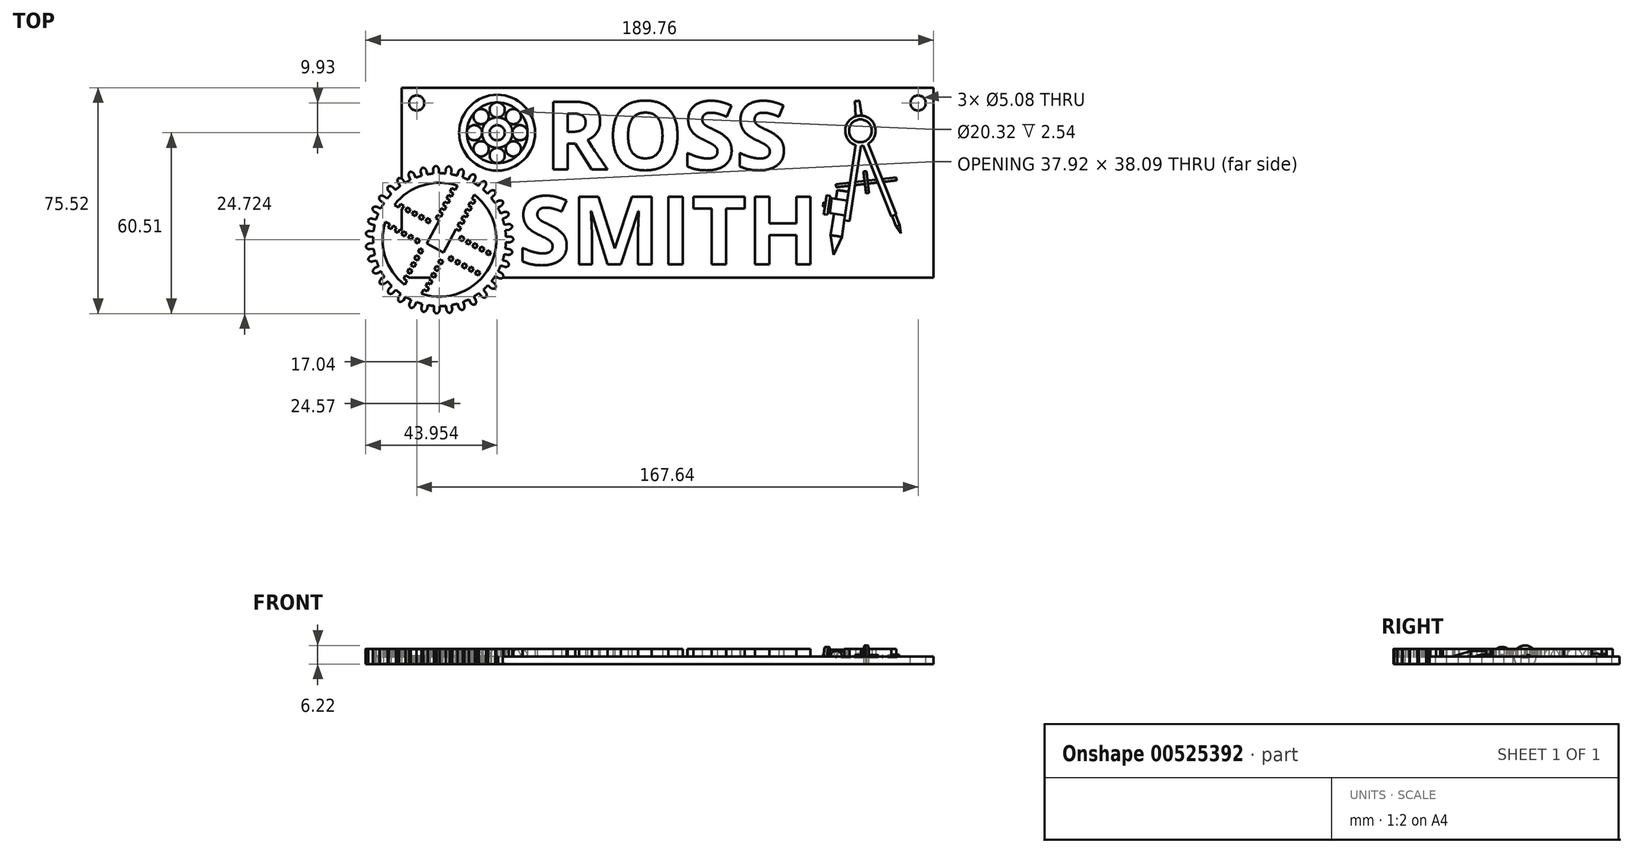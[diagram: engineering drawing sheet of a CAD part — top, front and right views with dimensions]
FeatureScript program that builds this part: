
annotation { "Feature Type Name" : "Feature", "Feature Type Description" : "" }
export const myFeature = defineFeature(function(context is Context, id is Id, definition is map)
    precondition{}
    {
        {
            var Q0;
            Q0=qCreatedBy(makeId("Top.planeOp"),FACE);
            var sketch = newSketch(context, id + "F0", { "sketchPlane" : qUnion([Q0])});
            skLineSegment(sketch, "E0.bottom", {"start": v(88.9, 31.75) * mm, "end": v(-88.9, 31.75) * mm});
            skLineSegment(sketch, "E0.top", {"start": v(88.9, -31.75) * mm, "end": v(-88.9, -31.75) * mm});
            skLineSegment(sketch, "E0.left", {"start": v(88.9, 31.75) * mm, "end": v(88.9, -31.75) * mm});
            skLineSegment(sketch, "E0.right", {"start": v(-88.9, 31.75) * mm, "end": v(-88.9, -31.75) * mm});
            skPoint(sketch, "E0.middle", {"position": v(0, 0) * mm});
            skSolve(sketch);
        }
        {
            var Q0;
            Q0=makeQuery(id+"F0.imprint","IMPRINT",FACE,{"disambiguationData":[TD([[makeQuery(id+"F0.imprint","IMPRINT",EDGE,{"derivedFrom":sQuery(id+"F0.wireOp",EDGE,"E0.bottom")}),1.0]])]});
            extrude(context, id + "F1", {"entities" : qUnion([Q0]), "depth" : 2.54 * mm, "offsetDistance" : 25.4 * mm});
        }
        {
            var Q0;
            Q0=makeQuery(id+"F1.opExtrude","CAP_FACE",FACE,{"disambiguationData":[OSD([sQuery(id+"F0.wireOp",EDGE,"E0.bottom"),sQuery(id+"F0.wireOp",EDGE,"E0.top"),sQuery(id+"F0.wireOp",EDGE,"E0.left"),sQuery(id+"F0.wireOp",EDGE,"E0.right")])],"isStart":false});
            var sketch = newSketch(context, id + "F2", { "sketchPlane" : qUnion([Q0])});
            skLineSegment(sketch, "E1.left", {"start": v(-49.9, -4.45) * mm, "end": v(-49.9, -27.3) * mm});
            skText(sketch, "E2", { "text": "ROSS", "fontName": "OpenSans-Bold.ttf"});
            skText(sketch, "E3", { "text": "SMITH", "fontName": "OpenSans-Bold.ttf"});
            const initialGuessF2  = {"E2": [-0.041, 0.00445, 1, 0, 0.02286], "E3": [-0.0499, -0.0273, 1, 0, 0.02286]};
            skSetInitialGuess(sketch, initialGuessF2);
            skSolve(sketch);
        }
        {
            var Q0;
            Q0 = qSketchRegion(id + "F2", true);
            extrude(context, id + "F3", {"entities" : qUnion([Q0]), "operationType" : NewBodyOperationType.ADD, "depth" : 2.54 * mm, "offsetDistance" : 25.4 * mm});
        }
        {
            var Q0;
            {var subQ0=sQuery(id+"F0.wireOp",EDGE,"E0.left");var subQ1=sQuery(id+"F0.wireOp",EDGE,"E0.top");var subQ2=sQuery(id+"F0.wireOp",EDGE,"E0.right");var subQ3=sQuery(id+"F0.wireOp",EDGE,"E0.bottom");Q0=makeQuery(id+"F3.boolean.opBoolean","SPLIT",FACE,{"disambiguationData":[TD([makeQuery(id+"F1.opExtrude","SWEPT_FACE",FACE,{"disambiguationData":[OSD([subQ3])]})])],"derivedFrom":makeQuery(id+"F1.opExtrude","CAP_FACE",FACE,{"disambiguationData":[OSD([subQ3,subQ1,subQ0,subQ2])],"isStart":false})});}
            var sketch = newSketch(context, id + "F4", { "sketchPlane" : qUnion([Q0])});
            skCircle(sketch, "E4", {"center": v(-76.2, -19.05) * mm, "radius": 22.23 * mm});
            skLineSegment(sketch, "E5.bottom", {"start": v(-71.9, -17.74) * mm, "end": v(-77.51, -14.76) * mm});
            skLineSegment(sketch, "E5.top", {"start": v(-74.89, -23.34) * mm, "end": v(-80.5, -20.36) * mm});
            skLineSegment(sketch, "E5.left", {"start": v(-71.9, -17.74) * mm, "end": v(-74.89, -23.34) * mm});
            skLineSegment(sketch, "E5.right", {"start": v(-77.51, -14.76) * mm, "end": v(-80.5, -20.36) * mm});
            skCircle(sketch, "E6", {"center": v(-76.2, -19.05) * mm, "radius": 19.05 * mm});
            skLineSegment(sketch, "E7", {"start": v(-77.51, -14.76) * mm, "end": v(-70.19, -0.97) * mm});
            skLineSegment(sketch, "E8", {"start": v(-71.9, -17.74) * mm, "end": v(-64.58, -3.96) * mm});
            skLineSegment(sketch, "E9.bottom", {"start": v(-71.9, -17.74) * mm, "end": v(-70.78, -18.33) * mm});
            skLineSegment(sketch, "E9.top", {"start": v(-71.3, -16.62) * mm, "end": v(-70.19, -17.21) * mm});
            skLineSegment(sketch, "E9.left", {"start": v(-71.9, -17.74) * mm, "end": v(-71.3, -16.62) * mm});
            skLineSegment(sketch, "E9.right", {"start": v(-70.78, -18.33) * mm, "end": v(-70.19, -17.21) * mm});
            skLineSegment(sketch, "E10.bottom", {"start": v(-77.51, -14.76) * mm, "end": v(-78.63, -14.16) * mm});
            skLineSegment(sketch, "E10.top", {"start": v(-76.92, -13.63) * mm, "end": v(-78.04, -13.04) * mm});
            skLineSegment(sketch, "E10.left", {"start": v(-77.51, -14.76) * mm, "end": v(-76.92, -13.63) * mm});
            skLineSegment(sketch, "E10.right", {"start": v(-78.63, -14.16) * mm, "end": v(-78.04, -13.04) * mm});
            skLineSegment(sketch, "E11.0.1.0", {"start": v(-70.71, -15.5) * mm, "end": v(-69.6, -16.1) * mm});
            skLineSegment(sketch, "E11.0.1.1", {"start": v(-70.12, -14.37) * mm, "end": v(-69, -14.97) * mm});
            skLineSegment(sketch, "E11.0.1.2", {"start": v(-69.6, -16.1) * mm, "end": v(-69, -14.97) * mm});
            skLineSegment(sketch, "E11.0.1.3", {"start": v(-75.72, -11.4) * mm, "end": v(-76.85, -10.8) * mm});
            skLineSegment(sketch, "E11.0.1.4", {"start": v(-77.44, -11.92) * mm, "end": v(-76.85, -10.8) * mm});
            skLineSegment(sketch, "E11.0.1.5", {"start": v(-76.32, -12.51) * mm, "end": v(-77.44, -11.92) * mm});
            skLineSegment(sketch, "E11.0.2.0", {"start": v(-69.52, -13.25) * mm, "end": v(-68.4, -13.85) * mm});
            skLineSegment(sketch, "E11.0.2.1", {"start": v(-68.92, -12.13) * mm, "end": v(-67.8, -12.73) * mm});
            skLineSegment(sketch, "E11.0.2.2", {"start": v(-68.4, -13.85) * mm, "end": v(-67.8, -12.73) * mm});
            skLineSegment(sketch, "E11.0.2.3", {"start": v(-74.53, -9.15) * mm, "end": v(-75.65, -8.55) * mm});
            skLineSegment(sketch, "E11.0.2.4", {"start": v(-76.25, -9.67) * mm, "end": v(-75.65, -8.55) * mm});
            skLineSegment(sketch, "E11.0.2.5", {"start": v(-75.13, -10.27) * mm, "end": v(-76.25, -9.67) * mm});
            skLineSegment(sketch, "E11.0.3.0", {"start": v(-68.33, -11) * mm, "end": v(-67.2, -11.6) * mm});
            skLineSegment(sketch, "E11.0.3.1", {"start": v(-67.73, -9.89) * mm, "end": v(-66.61, -10.48) * mm});
            skLineSegment(sketch, "E11.0.3.2", {"start": v(-67.2, -11.6) * mm, "end": v(-66.61, -10.48) * mm});
            skLineSegment(sketch, "E11.0.3.3", {"start": v(-73.34, -6.9) * mm, "end": v(-74.46, -6.31) * mm});
            skLineSegment(sketch, "E11.0.3.4", {"start": v(-75.06, -7.43) * mm, "end": v(-74.46, -6.31) * mm});
            skLineSegment(sketch, "E11.0.3.5", {"start": v(-73.94, -8.03) * mm, "end": v(-75.06, -7.43) * mm});
            skLineSegment(sketch, "E11.0.4.0", {"start": v(-67.14, -8.77) * mm, "end": v(-66.01, -9.36) * mm});
            skLineSegment(sketch, "E11.0.4.1", {"start": v(-66.54, -7.65) * mm, "end": v(-65.42, -8.24) * mm});
            skLineSegment(sketch, "E11.0.4.2", {"start": v(-66.01, -9.36) * mm, "end": v(-65.42, -8.24) * mm});
            skLineSegment(sketch, "E11.0.4.3", {"start": v(-72.15, -4.66) * mm, "end": v(-73.27, -4.07) * mm});
            skLineSegment(sketch, "E11.0.4.4", {"start": v(-73.86, -5.19) * mm, "end": v(-73.27, -4.07) * mm});
            skLineSegment(sketch, "E11.0.4.5", {"start": v(-72.74, -5.79) * mm, "end": v(-73.86, -5.19) * mm});
            skLineSegment(sketch, "E11.0.5.0", {"start": v(-65.94, -6.52) * mm, "end": v(-64.82, -7.12) * mm});
            skLineSegment(sketch, "E11.0.5.1", {"start": v(-65.35, -5.4) * mm, "end": v(-64.23, -6) * mm});
            skLineSegment(sketch, "E11.0.5.2", {"start": v(-64.82, -7.12) * mm, "end": v(-64.23, -6) * mm});
            skLineSegment(sketch, "E11.0.5.3", {"start": v(-70.95, -2.42) * mm, "end": v(-72.08, -1.83) * mm});
            skLineSegment(sketch, "E11.0.5.4", {"start": v(-72.67, -2.95) * mm, "end": v(-72.08, -1.83) * mm});
            skLineSegment(sketch, "E11.0.5.5", {"start": v(-71.55, -3.54) * mm, "end": v(-72.67, -2.95) * mm});
            skLineSegment(sketch, "E11.direction1", {"start": v(-78.63, -14.16) * mm, "end": v(-56.2, -26.08) * mm, "construction": true});
            skLineSegment(sketch, "E11.direction2", {"start": v(-78.63, -14.16) * mm, "end": v(-77.44, -11.92) * mm, "construction": true});
            skLineSegment(sketch, "E12.1.0", {"start": v(-77.51, -14.76) * mm, "end": v(-91.3, -7.43) * mm});
            skLineSegment(sketch, "E12.1.1", {"start": v(-80.5, -20.36) * mm, "end": v(-94.28, -13.04) * mm});
            skLineSegment(sketch, "E12.1.2", {"start": v(-91.7, -14.4) * mm, "end": v(-92.3, -15.52) * mm});
            skLineSegment(sketch, "E12.1.3", {"start": v(-82.74, -19.17) * mm, "end": v(-83.33, -20.3) * mm});
            skLineSegment(sketch, "E12.1.4", {"start": v(-83.64, -10.06) * mm, "end": v(-84.77, -9.46) * mm});
            skLineSegment(sketch, "E12.1.5", {"start": v(-90.59, -15) * mm, "end": v(-91.18, -16.12) * mm});
            skLineSegment(sketch, "E12.1.6", {"start": v(-80.5, -20.36) * mm, "end": v(-81.1, -21.48) * mm});
            skLineSegment(sketch, "E12.1.8", {"start": v(-92.3, -15.52) * mm, "end": v(-93.42, -14.93) * mm});
            skLineSegment(sketch, "E12.1.11", {"start": v(-80.5, -20.36) * mm, "end": v(-81.62, -19.77) * mm});
            skLineSegment(sketch, "E12.1.12", {"start": v(-85.58, -19.1) * mm, "end": v(-86.7, -18.5) * mm});
            skLineSegment(sketch, "E12.1.13", {"start": v(-89.46, -15.6) * mm, "end": v(-90.06, -16.71) * mm});
            skLineSegment(sketch, "E12.1.14", {"start": v(-88.13, -7.67) * mm, "end": v(-89.25, -7.08) * mm});
            skLineSegment(sketch, "E12.1.15", {"start": v(-87.82, -17.9) * mm, "end": v(-88.94, -17.31) * mm});
            skLineSegment(sketch, "E12.1.16", {"start": v(-81.1, -21.48) * mm, "end": v(-83.33, -20.3) * mm, "construction": true});
            skLineSegment(sketch, "E12.1.17", {"start": v(-88.34, -16.19) * mm, "end": v(-88.94, -17.31) * mm});
            skLineSegment(sketch, "E12.1.18", {"start": v(-83.86, -18.57) * mm, "end": v(-84.45, -19.7) * mm});
            skLineSegment(sketch, "E12.1.19", {"start": v(-81.4, -11.25) * mm, "end": v(-82.52, -10.65) * mm});
            skLineSegment(sketch, "E12.1.20", {"start": v(-87.22, -16.79) * mm, "end": v(-87.82, -17.9) * mm});
            skLineSegment(sketch, "E12.1.21", {"start": v(-92.83, -13.8) * mm, "end": v(-93.42, -14.93) * mm});
            skLineSegment(sketch, "E12.1.22", {"start": v(-84.98, -17.98) * mm, "end": v(-85.58, -19.1) * mm});
            skLineSegment(sketch, "E12.1.23", {"start": v(-83.33, -20.3) * mm, "end": v(-84.45, -19.7) * mm});
            skLineSegment(sketch, "E12.1.24", {"start": v(-79.16, -12.44) * mm, "end": v(-80.28, -11.85) * mm});
            skLineSegment(sketch, "E12.1.25", {"start": v(-86.1, -17.38) * mm, "end": v(-86.7, -18.5) * mm});
            skLineSegment(sketch, "E12.1.26", {"start": v(-81.62, -19.77) * mm, "end": v(-82.21, -20.89) * mm});
            skLineSegment(sketch, "E12.1.27", {"start": v(-84.24, -11.18) * mm, "end": v(-83.64, -10.06) * mm});
            skLineSegment(sketch, "E12.1.28", {"start": v(-81.1, -21.48) * mm, "end": v(-82.21, -20.89) * mm});
            skLineSegment(sketch, "E12.1.29", {"start": v(-87.6, -9.4) * mm, "end": v(-87, -8.27) * mm});
            skLineSegment(sketch, "E12.1.30", {"start": v(-83.12, -11.77) * mm, "end": v(-82.52, -10.65) * mm});
            skLineSegment(sketch, "E12.1.31", {"start": v(-79.76, -13.56) * mm, "end": v(-79.16, -12.44) * mm});
            skLineSegment(sketch, "E12.1.32", {"start": v(-82, -12.37) * mm, "end": v(-81.4, -11.25) * mm});
            skLineSegment(sketch, "E12.1.33", {"start": v(-88.73, -8.8) * mm, "end": v(-88.13, -7.67) * mm});
            skLineSegment(sketch, "E12.1.34", {"start": v(-85.36, -10.58) * mm, "end": v(-84.77, -9.46) * mm});
            skLineSegment(sketch, "E12.1.35", {"start": v(-80.88, -12.97) * mm, "end": v(-80.28, -11.85) * mm});
            skLineSegment(sketch, "E12.1.36", {"start": v(-86.48, -9.99) * mm, "end": v(-85.89, -8.86) * mm});
            skLineSegment(sketch, "E12.1.37", {"start": v(-89.85, -8.2) * mm, "end": v(-89.25, -7.08) * mm});
            skLineSegment(sketch, "E12.1.40", {"start": v(-90.06, -16.71) * mm, "end": v(-91.18, -16.12) * mm});
            skLineSegment(sketch, "E12.1.41", {"start": v(-85.89, -8.86) * mm, "end": v(-87, -8.27) * mm});
            skLineSegment(sketch, "E12.2.0", {"start": v(-80.5, -20.36) * mm, "end": v(-87.82, -34.14) * mm});
            skLineSegment(sketch, "E12.2.1", {"start": v(-74.89, -23.34) * mm, "end": v(-82.21, -37.13) * mm});
            skLineSegment(sketch, "E12.2.2", {"start": v(-80.85, -34.56) * mm, "end": v(-79.73, -35.15) * mm});
            skLineSegment(sketch, "E12.2.3", {"start": v(-76.08, -25.59) * mm, "end": v(-74.96, -26.18) * mm});
            skLineSegment(sketch, "E12.2.4", {"start": v(-85.2, -26.5) * mm, "end": v(-85.79, -27.62) * mm});
            skLineSegment(sketch, "E12.2.5", {"start": v(-80.25, -33.44) * mm, "end": v(-79.13, -34.03) * mm});
            skLineSegment(sketch, "E12.2.6", {"start": v(-74.89, -23.34) * mm, "end": v(-73.77, -23.94) * mm});
            skLineSegment(sketch, "E12.2.7", {"start": v(-81.62, -19.77) * mm, "end": v(-82.21, -20.89) * mm});
            skLineSegment(sketch, "E12.2.8", {"start": v(-79.73, -35.15) * mm, "end": v(-80.32, -36.27) * mm});
            skLineSegment(sketch, "E12.2.9", {"start": v(-80.5, -20.36) * mm, "end": v(-81.1, -21.48) * mm});
            skLineSegment(sketch, "E12.2.10", {"start": v(-80.5, -20.36) * mm, "end": v(-74.89, -23.34) * mm});
            skLineSegment(sketch, "E12.2.11", {"start": v(-74.89, -23.34) * mm, "end": v(-75.48, -24.47) * mm});
            skLineSegment(sketch, "E12.2.12", {"start": v(-76.15, -28.43) * mm, "end": v(-76.75, -29.55) * mm});
            skLineSegment(sketch, "E12.2.13", {"start": v(-79.66, -32.31) * mm, "end": v(-78.54, -32.91) * mm});
            skLineSegment(sketch, "E12.2.14", {"start": v(-87.58, -30.98) * mm, "end": v(-88.17, -32.1) * mm});
            skLineSegment(sketch, "E12.2.15", {"start": v(-77.34, -30.67) * mm, "end": v(-77.94, -31.79) * mm});
            skLineSegment(sketch, "E12.2.16", {"start": v(-73.77, -23.94) * mm, "end": v(-74.96, -26.18) * mm, "construction": true});
            skLineSegment(sketch, "E12.2.17", {"start": v(-79.06, -31.2) * mm, "end": v(-77.94, -31.79) * mm});
            skLineSegment(sketch, "E12.2.18", {"start": v(-76.68, -26.7) * mm, "end": v(-75.55, -27.3) * mm});
            skLineSegment(sketch, "E12.2.19", {"start": v(-84, -24.25) * mm, "end": v(-84.6, -25.37) * mm});
            skLineSegment(sketch, "E12.2.20", {"start": v(-78.46, -30.07) * mm, "end": v(-77.34, -30.67) * mm});
            skLineSegment(sketch, "E12.2.21", {"start": v(-81.45, -35.68) * mm, "end": v(-80.32, -36.27) * mm});
            skLineSegment(sketch, "E12.2.22", {"start": v(-77.27, -27.83) * mm, "end": v(-76.15, -28.43) * mm});
            skLineSegment(sketch, "E12.2.23", {"start": v(-74.96, -26.18) * mm, "end": v(-75.55, -27.3) * mm});
            skLineSegment(sketch, "E12.2.24", {"start": v(-82.8, -22) * mm, "end": v(-83.4, -23.13) * mm});
            skLineSegment(sketch, "E12.2.25", {"start": v(-77.87, -28.95) * mm, "end": v(-76.75, -29.55) * mm});
            skLineSegment(sketch, "E12.2.26", {"start": v(-75.48, -24.47) * mm, "end": v(-74.36, -25.06) * mm});
            skLineSegment(sketch, "E12.2.27", {"start": v(-84.07, -27.1) * mm, "end": v(-85.2, -26.5) * mm});
            skLineSegment(sketch, "E12.2.28", {"start": v(-73.77, -23.94) * mm, "end": v(-74.36, -25.06) * mm});
            skLineSegment(sketch, "E12.2.29", {"start": v(-85.86, -30.45) * mm, "end": v(-86.98, -29.86) * mm});
            skLineSegment(sketch, "E12.2.30", {"start": v(-83.48, -25.97) * mm, "end": v(-84.6, -25.37) * mm});
            skLineSegment(sketch, "E12.2.31", {"start": v(-81.69, -22.6) * mm, "end": v(-82.8, -22) * mm});
            skLineSegment(sketch, "E12.2.32", {"start": v(-82.88, -24.85) * mm, "end": v(-84, -24.25) * mm});
            skLineSegment(sketch, "E12.2.33", {"start": v(-86.46, -31.58) * mm, "end": v(-87.58, -30.98) * mm});
            skLineSegment(sketch, "E12.2.34", {"start": v(-84.67, -28.21) * mm, "end": v(-85.79, -27.62) * mm});
            skLineSegment(sketch, "E12.2.35", {"start": v(-82.28, -23.73) * mm, "end": v(-83.4, -23.13) * mm});
            skLineSegment(sketch, "E12.2.36", {"start": v(-85.26, -29.33) * mm, "end": v(-86.39, -28.74) * mm});
            skLineSegment(sketch, "E12.2.37", {"start": v(-87.05, -32.7) * mm, "end": v(-88.17, -32.1) * mm});
            skLineSegment(sketch, "E12.2.38", {"start": v(-81.1, -21.48) * mm, "end": v(-82.21, -20.89) * mm});
            skLineSegment(sketch, "E12.2.39", {"start": v(-80.5, -20.36) * mm, "end": v(-81.62, -19.77) * mm});
            skLineSegment(sketch, "E12.2.40", {"start": v(-78.54, -32.91) * mm, "end": v(-79.13, -34.03) * mm});
            skLineSegment(sketch, "E12.2.41", {"start": v(-86.39, -28.74) * mm, "end": v(-86.98, -29.86) * mm});
            skLineSegment(sketch, "E12.3.0", {"start": v(-74.89, -23.34) * mm, "end": v(-61.1, -30.67) * mm});
            skLineSegment(sketch, "E12.3.1", {"start": v(-71.9, -17.74) * mm, "end": v(-58.12, -25.06) * mm});
            skLineSegment(sketch, "E12.3.2", {"start": v(-60.7, -23.7) * mm, "end": v(-60.1, -22.58) * mm});
            skLineSegment(sketch, "E12.3.3", {"start": v(-69.66, -18.93) * mm, "end": v(-69.07, -17.8) * mm});
            skLineSegment(sketch, "E12.3.4", {"start": v(-68.76, -28.04) * mm, "end": v(-67.63, -28.64) * mm});
            skLineSegment(sketch, "E12.3.5", {"start": v(-61.81, -23.1) * mm, "end": v(-61.22, -21.98) * mm});
            skLineSegment(sketch, "E12.3.7", {"start": v(-75.48, -24.47) * mm, "end": v(-74.36, -25.06) * mm});
            skLineSegment(sketch, "E12.3.8", {"start": v(-60.1, -22.58) * mm, "end": v(-58.98, -23.17) * mm});
            skLineSegment(sketch, "E12.3.9", {"start": v(-74.89, -23.34) * mm, "end": v(-73.77, -23.94) * mm});
            skLineSegment(sketch, "E12.3.10", {"start": v(-74.89, -23.34) * mm, "end": v(-71.9, -17.74) * mm});
            skLineSegment(sketch, "E12.3.12", {"start": v(-66.82, -19) * mm, "end": v(-65.7, -19.6) * mm});
            skLineSegment(sketch, "E12.3.13", {"start": v(-62.94, -22.5) * mm, "end": v(-62.34, -21.39) * mm});
            skLineSegment(sketch, "E12.3.14", {"start": v(-64.27, -30.43) * mm, "end": v(-63.15, -31.02) * mm});
            skLineSegment(sketch, "E12.3.15", {"start": v(-64.58, -20.2) * mm, "end": v(-63.46, -20.79) * mm});
            skLineSegment(sketch, "E12.3.16", {"start": v(-71.3, -16.62) * mm, "end": v(-69.07, -17.8) * mm, "construction": true});
            skLineSegment(sketch, "E12.3.17", {"start": v(-64.06, -21.91) * mm, "end": v(-63.46, -20.79) * mm});
            skLineSegment(sketch, "E12.3.18", {"start": v(-68.54, -19.53) * mm, "end": v(-67.95, -18.4) * mm});
            skLineSegment(sketch, "E12.3.19", {"start": v(-71, -26.85) * mm, "end": v(-69.88, -27.45) * mm});
            skLineSegment(sketch, "E12.3.20", {"start": v(-65.18, -21.31) * mm, "end": v(-64.58, -20.2) * mm});
            skLineSegment(sketch, "E12.3.21", {"start": v(-59.57, -24.3) * mm, "end": v(-58.98, -23.17) * mm});
            skLineSegment(sketch, "E12.3.22", {"start": v(-67.42, -20.12) * mm, "end": v(-66.82, -19) * mm});
            skLineSegment(sketch, "E12.3.23", {"start": v(-69.07, -17.8) * mm, "end": v(-67.95, -18.4) * mm});
            skLineSegment(sketch, "E12.3.24", {"start": v(-73.24, -25.66) * mm, "end": v(-72.12, -26.25) * mm});
            skLineSegment(sketch, "E12.3.25", {"start": v(-66.3, -20.72) * mm, "end": v(-65.7, -19.6) * mm});
            skLineSegment(sketch, "E12.3.27", {"start": v(-68.16, -26.92) * mm, "end": v(-68.76, -28.04) * mm});
            skLineSegment(sketch, "E12.3.29", {"start": v(-64.8, -28.7) * mm, "end": v(-65.4, -29.83) * mm});
            skLineSegment(sketch, "E12.3.30", {"start": v(-69.28, -26.33) * mm, "end": v(-69.88, -27.45) * mm});
            skLineSegment(sketch, "E12.3.31", {"start": v(-72.64, -24.54) * mm, "end": v(-73.24, -25.66) * mm});
            skLineSegment(sketch, "E12.3.32", {"start": v(-70.4, -25.73) * mm, "end": v(-71, -26.85) * mm});
            skLineSegment(sketch, "E12.3.33", {"start": v(-63.67, -29.3) * mm, "end": v(-64.27, -30.43) * mm});
            skLineSegment(sketch, "E12.3.34", {"start": v(-67.04, -27.52) * mm, "end": v(-67.63, -28.64) * mm});
            skLineSegment(sketch, "E12.3.35", {"start": v(-71.52, -25.13) * mm, "end": v(-72.12, -26.25) * mm});
            skLineSegment(sketch, "E12.3.36", {"start": v(-65.92, -28.11) * mm, "end": v(-66.51, -29.24) * mm});
            skLineSegment(sketch, "E12.3.37", {"start": v(-62.55, -29.9) * mm, "end": v(-63.15, -31.02) * mm});
            skLineSegment(sketch, "E12.3.38", {"start": v(-73.77, -23.94) * mm, "end": v(-74.36, -25.06) * mm});
            skLineSegment(sketch, "E12.3.39", {"start": v(-74.89, -23.34) * mm, "end": v(-75.48, -24.47) * mm});
            skLineSegment(sketch, "E12.3.40", {"start": v(-62.34, -21.39) * mm, "end": v(-61.22, -21.98) * mm});
            skLineSegment(sketch, "E12.3.41", {"start": v(-66.51, -29.24) * mm, "end": v(-65.4, -29.83) * mm});
            skLineSegment(sketch, "E13", {"start": v(-66.62, 1) * mm, "end": v(-64.93, 0.1) * mm});
            skPoint(sketch, "E14.positionSnap0", {"position": v(-74.7, -16.25) * mm});
            skPoint(sketch, "E15", {"position": v(-64.58, 2.8) * mm});
            skPoint(sketch, "E15.positionSnap0", {"position": v(-65.77, 0.55) * mm});
            skLineSegment(sketch, "E16", {"start": v(-66.62, 1) * mm, "end": v(-66.02, 2.12) * mm});
            skLineSegment(sketch, "E17", {"start": v(-64.93, 0.1) * mm, "end": v(-64.34, 1.23) * mm});
            skArc(sketch, "E18", {"start": v(-64.58, 2.8) * mm, "mid": v(-65.41, 2.7) * mm, "end": v(-66.02, 2.12) * mm});
            skArc(sketch, "E19", {"start": v(-64.34, 1.23) * mm, "mid": v(-64.2, 2.05) * mm, "end": v(-64.58, 2.8) * mm});
            skArc(sketch, "E20.1.0", {"start": v(-68.15, 3.02) * mm, "mid": v(-68.16, 3.86) * mm, "end": v(-68.67, 4.52) * mm});
            skArc(sketch, "E20.1.1", {"start": v(-68.67, 4.52) * mm, "mid": v(-69.47, 4.28) * mm, "end": v(-69.96, 3.6) * mm});
            skLineSegment(sketch, "E20.1.2", {"start": v(-70.35, 2.4) * mm, "end": v(-69.96, 3.6) * mm});
            skLineSegment(sketch, "E20.1.3", {"start": v(-68.54, 1.81) * mm, "end": v(-68.15, 3.02) * mm});
            skArc(sketch, "E20.2.0", {"start": v(-72.22, 4.1) * mm, "mid": v(-72.38, 4.93) * mm, "end": v(-73, 5.49) * mm});
            skArc(sketch, "E20.2.1", {"start": v(-73, 5.49) * mm, "mid": v(-73.74, 5.1) * mm, "end": v(-74.1, 4.35) * mm});
            skLineSegment(sketch, "E20.2.2", {"start": v(-74.27, 3.1) * mm, "end": v(-74.1, 4.35) * mm});
            skLineSegment(sketch, "E20.2.3", {"start": v(-72.38, 2.84) * mm, "end": v(-72.22, 4.1) * mm});
            skArc(sketch, "E20.3.0", {"start": v(-76.42, 4.44) * mm, "mid": v(-76.72, 5.22) * mm, "end": v(-77.43, 5.66) * mm});
            skArc(sketch, "E20.3.1", {"start": v(-77.43, 5.66) * mm, "mid": v(-78.1, 5.15) * mm, "end": v(-78.32, 4.35) * mm});
            skLineSegment(sketch, "E20.3.2", {"start": v(-78.26, 3.08) * mm, "end": v(-78.32, 4.35) * mm});
            skLineSegment(sketch, "E20.3.3", {"start": v(-76.35, 3.17) * mm, "end": v(-76.42, 4.44) * mm});
            skArc(sketch, "E20.4.0", {"start": v(-80.6, 4.03) * mm, "mid": v(-81.05, 4.74) * mm, "end": v(-81.82, 5.05) * mm});
            skArc(sketch, "E20.4.1", {"start": v(-81.82, 5.05) * mm, "mid": v(-82.39, 4.43) * mm, "end": v(-82.46, 3.6) * mm});
            skLineSegment(sketch, "E20.4.2", {"start": v(-82.17, 2.36) * mm, "end": v(-82.46, 3.6) * mm});
            skLineSegment(sketch, "E20.4.3", {"start": v(-80.32, 2.79) * mm, "end": v(-80.6, 4.03) * mm});
            skArc(sketch, "E20.5.0", {"start": v(-84.66, 2.87) * mm, "mid": v(-85.22, 3.5) * mm, "end": v(-86.04, 3.66) * mm});
            skArc(sketch, "E20.5.1", {"start": v(-86.04, 3.66) * mm, "mid": v(-86.48, 2.94) * mm, "end": v(-86.4, 2.11) * mm});
            skLineSegment(sketch, "E20.5.2", {"start": v(-85.9, 0.95) * mm, "end": v(-86.4, 2.11) * mm});
            skLineSegment(sketch, "E20.5.3", {"start": v(-84.15, 1.7) * mm, "end": v(-84.66, 2.87) * mm});
            skArc(sketch, "E20.6.0", {"start": v(-88.44, 1) * mm, "mid": v(-89.1, 1.52) * mm, "end": v(-89.93, 1.53) * mm});
            skArc(sketch, "E20.6.1", {"start": v(-89.93, 1.53) * mm, "mid": v(-90.24, 0.76) * mm, "end": v(-90.02, -0.05) * mm});
            skLineSegment(sketch, "E20.6.2", {"start": v(-89.32, -1.1) * mm, "end": v(-90.02, -0.05) * mm});
            skLineSegment(sketch, "E20.6.3", {"start": v(-87.73, -0.05) * mm, "end": v(-88.44, 1) * mm});
            skArc(sketch, "E20.7.0", {"start": v(-91.82, -1.5) * mm, "mid": v(-92.56, -1.11) * mm, "end": v(-93.39, -1.25) * mm});
            skArc(sketch, "E20.7.1", {"start": v(-93.39, -1.25) * mm, "mid": v(-93.55, -2.07) * mm, "end": v(-93.2, -2.82) * mm});
            skLineSegment(sketch, "E20.7.2", {"start": v(-92.3, -3.74) * mm, "end": v(-93.2, -2.82) * mm});
            skLineSegment(sketch, "E20.7.3", {"start": v(-90.94, -2.41) * mm, "end": v(-91.82, -1.5) * mm});
            skArc(sketch, "E20.8.0", {"start": v(-94.7, -4.57) * mm, "mid": v(-95.5, -4.32) * mm, "end": v(-96.3, -4.6) * mm});
            skArc(sketch, "E20.8.1", {"start": v(-96.3, -4.6) * mm, "mid": v(-96.3, -5.44) * mm, "end": v(-95.82, -6.12) * mm});
            skLineSegment(sketch, "E20.8.2", {"start": v(-94.78, -6.86) * mm, "end": v(-95.82, -6.12) * mm});
            skLineSegment(sketch, "E20.8.3", {"start": v(-93.67, -5.31) * mm, "end": v(-94.7, -4.57) * mm});
            skArc(sketch, "E20.9.0", {"start": v(-97, -8.1) * mm, "mid": v(-97.82, -8) * mm, "end": v(-98.55, -8.42) * mm});
            skArc(sketch, "E20.9.1", {"start": v(-98.55, -8.42) * mm, "mid": v(-98.41, -9.25) * mm, "end": v(-97.8, -9.83) * mm});
            skLineSegment(sketch, "E20.9.2", {"start": v(-96.66, -10.37) * mm, "end": v(-97.8, -9.83) * mm});
            skLineSegment(sketch, "E20.9.3", {"start": v(-95.84, -8.65) * mm, "end": v(-97, -8.1) * mm});
            skArc(sketch, "E20.10.0", {"start": v(-98.61, -12) * mm, "mid": v(-99.45, -12.05) * mm, "end": v(-100.08, -12.58) * mm});
            skArc(sketch, "E20.10.1", {"start": v(-100.08, -12.58) * mm, "mid": v(-99.8, -13.37) * mm, "end": v(-99.1, -13.84) * mm});
            skLineSegment(sketch, "E20.10.2", {"start": v(-97.88, -14.17) * mm, "end": v(-99.1, -13.84) * mm});
            skLineSegment(sketch, "E20.10.3", {"start": v(-97.38, -12.33) * mm, "end": v(-98.61, -12) * mm});
            skArc(sketch, "E20.11.0", {"start": v(-99.5, -16.11) * mm, "mid": v(-100.32, -16.3) * mm, "end": v(-100.86, -16.95) * mm});
            skArc(sketch, "E20.11.1", {"start": v(-100.86, -16.95) * mm, "mid": v(-100.44, -17.68) * mm, "end": v(-99.67, -18) * mm});
            skLineSegment(sketch, "E20.11.2", {"start": v(-98.4, -18.12) * mm, "end": v(-99.67, -18) * mm});
            skLineSegment(sketch, "E20.11.3", {"start": v(-98.24, -16.22) * mm, "end": v(-99.5, -16.11) * mm});
            skArc(sketch, "E20.12.0", {"start": v(-99.66, -20.32) * mm, "mid": v(-100.42, -20.66) * mm, "end": v(-100.83, -21.39) * mm});
            skArc(sketch, "E20.12.1", {"start": v(-100.83, -21.39) * mm, "mid": v(-100.3, -22.03) * mm, "end": v(-99.48, -22.22) * mm});
            skLineSegment(sketch, "E20.12.2", {"start": v(-98.21, -22.1) * mm, "end": v(-99.48, -22.22) * mm});
            skLineSegment(sketch, "E20.12.3", {"start": v(-98.4, -20.2) * mm, "end": v(-99.66, -20.32) * mm});
            skArc(sketch, "E20.13.0", {"start": v(-99.06, -24.49) * mm, "mid": v(-99.75, -24.96) * mm, "end": v(-100.02, -25.75) * mm});
            skArc(sketch, "E20.13.1", {"start": v(-100.02, -25.75) * mm, "mid": v(-99.38, -26.28) * mm, "end": v(-98.54, -26.32) * mm});
            skLineSegment(sketch, "E20.13.2", {"start": v(-97.32, -25.98) * mm, "end": v(-98.54, -26.32) * mm});
            skLineSegment(sketch, "E20.13.3", {"start": v(-97.83, -24.15) * mm, "end": v(-99.06, -24.49) * mm});
            skArc(sketch, "E20.14.0", {"start": v(-97.72, -28.48) * mm, "mid": v(-98.31, -29.07) * mm, "end": v(-98.44, -29.9) * mm});
            skArc(sketch, "E20.14.1", {"start": v(-98.44, -29.9) * mm, "mid": v(-97.71, -30.3) * mm, "end": v(-96.88, -30.2) * mm});
            skLineSegment(sketch, "E20.14.2", {"start": v(-95.74, -29.64) * mm, "end": v(-96.88, -30.2) * mm});
            skLineSegment(sketch, "E20.14.3", {"start": v(-96.58, -27.93) * mm, "end": v(-97.72, -28.48) * mm});
            skArc(sketch, "E20.15.0", {"start": v(-95.69, -32.17) * mm, "mid": v(-96.17, -32.86) * mm, "end": v(-96.15, -33.7) * mm});
            skArc(sketch, "E20.15.1", {"start": v(-96.15, -33.7) * mm, "mid": v(-95.36, -33.97) * mm, "end": v(-94.56, -33.7) * mm});
            skLineSegment(sketch, "E20.15.2", {"start": v(-93.54, -32.96) * mm, "end": v(-94.56, -33.7) * mm});
            skLineSegment(sketch, "E20.15.3", {"start": v(-94.66, -31.42) * mm, "end": v(-95.69, -32.17) * mm});
            skArc(sketch, "E20.16.0", {"start": v(-93.03, -35.44) * mm, "mid": v(-93.38, -36.2) * mm, "end": v(-93.21, -37.02) * mm});
            skArc(sketch, "E20.16.1", {"start": v(-93.21, -37.02) * mm, "mid": v(-92.38, -37.15) * mm, "end": v(-91.65, -36.75) * mm});
            skLineSegment(sketch, "E20.16.2", {"start": v(-90.77, -35.83) * mm, "end": v(-91.65, -36.75) * mm});
            skLineSegment(sketch, "E20.16.3", {"start": v(-92.16, -34.52) * mm, "end": v(-93.03, -35.44) * mm});
            skArc(sketch, "E20.17.0", {"start": v(-89.83, -38.18) * mm, "mid": v(-90.05, -39) * mm, "end": v(-89.73, -39.77) * mm});
            skArc(sketch, "E20.17.1", {"start": v(-89.73, -39.77) * mm, "mid": v(-88.9, -39.75) * mm, "end": v(-88.24, -39.23) * mm});
            skLineSegment(sketch, "E20.17.2", {"start": v(-87.54, -38.16) * mm, "end": v(-88.24, -39.23) * mm});
            skLineSegment(sketch, "E20.17.3", {"start": v(-89.14, -37.12) * mm, "end": v(-89.83, -38.18) * mm});
            skArc(sketch, "E20.18.0", {"start": v(-86.2, -40.31) * mm, "mid": v(-86.26, -41.14) * mm, "end": v(-85.81, -41.85) * mm});
            skArc(sketch, "E20.18.1", {"start": v(-85.81, -41.85) * mm, "mid": v(-85, -41.68) * mm, "end": v(-84.44, -41.05) * mm});
            skLineSegment(sketch, "E20.18.2", {"start": v(-83.95, -39.88) * mm, "end": v(-84.44, -41.05) * mm});
            skLineSegment(sketch, "E20.18.3", {"start": v(-85.7, -39.14) * mm, "end": v(-86.2, -40.31) * mm});
            skArc(sketch, "E20.19.0", {"start": v(-82.24, -41.75) * mm, "mid": v(-82.15, -42.59) * mm, "end": v(-81.59, -43.2) * mm});
            skArc(sketch, "E20.19.1", {"start": v(-81.59, -43.2) * mm, "mid": v(-80.81, -42.89) * mm, "end": v(-80.38, -42.17) * mm});
            skLineSegment(sketch, "E20.19.2", {"start": v(-80.1, -40.93) * mm, "end": v(-80.38, -42.17) * mm});
            skLineSegment(sketch, "E20.19.3", {"start": v(-81.96, -40.51) * mm, "end": v(-82.24, -41.75) * mm});
            skArc(sketch, "E20.20.0", {"start": v(-78.09, -42.47) * mm, "mid": v(-77.86, -43.27) * mm, "end": v(-77.19, -43.77) * mm});
            skArc(sketch, "E20.20.1", {"start": v(-77.19, -43.77) * mm, "mid": v(-76.48, -43.33) * mm, "end": v(-76.19, -42.54) * mm});
            skLineSegment(sketch, "E20.20.2", {"start": v(-76.14, -41.27) * mm, "end": v(-76.19, -42.54) * mm});
            skLineSegment(sketch, "E20.20.3", {"start": v(-78.04, -41.2) * mm, "end": v(-78.09, -42.47) * mm});
            skArc(sketch, "E20.21.0", {"start": v(-73.88, -42.43) * mm, "mid": v(-73.5, -43.18) * mm, "end": v(-72.76, -43.55) * mm});
            skArc(sketch, "E20.21.1", {"start": v(-72.76, -43.55) * mm, "mid": v(-72.14, -42.99) * mm, "end": v(-72, -42.16) * mm});
            skLineSegment(sketch, "E20.21.2", {"start": v(-72.17, -40.9) * mm, "end": v(-72, -42.16) * mm});
            skLineSegment(sketch, "E20.21.3", {"start": v(-74.05, -41.17) * mm, "end": v(-73.88, -42.43) * mm});
            skArc(sketch, "E20.22.0", {"start": v(-69.74, -41.64) * mm, "mid": v(-69.24, -42.3) * mm, "end": v(-68.44, -42.55) * mm});
            skArc(sketch, "E20.22.1", {"start": v(-68.44, -42.55) * mm, "mid": v(-67.93, -41.88) * mm, "end": v(-67.93, -41.04) * mm});
            skLineSegment(sketch, "E20.22.2", {"start": v(-68.33, -39.83) * mm, "end": v(-67.93, -41.04) * mm});
            skLineSegment(sketch, "E20.22.3", {"start": v(-70.14, -40.43) * mm, "end": v(-69.74, -41.64) * mm});
            skArc(sketch, "E20.23.0", {"start": v(-65.81, -40.12) * mm, "mid": v(-65.2, -40.7) * mm, "end": v(-64.37, -40.78) * mm});
            skArc(sketch, "E20.23.1", {"start": v(-64.37, -40.78) * mm, "mid": v(-64, -40.03) * mm, "end": v(-64.14, -39.21) * mm});
            skLineSegment(sketch, "E20.23.2", {"start": v(-64.75, -38.1) * mm, "end": v(-64.14, -39.21) * mm});
            skLineSegment(sketch, "E20.23.3", {"start": v(-66.42, -39) * mm, "end": v(-65.81, -40.12) * mm});
            skArc(sketch, "E20.24.0", {"start": v(-62.22, -37.93) * mm, "mid": v(-61.51, -38.38) * mm, "end": v(-60.68, -38.32) * mm});
            skArc(sketch, "E20.24.1", {"start": v(-60.68, -38.32) * mm, "mid": v(-60.44, -37.52) * mm, "end": v(-60.73, -36.73) * mm});
            skLineSegment(sketch, "E20.24.2", {"start": v(-61.53, -35.74) * mm, "end": v(-60.73, -36.73) * mm});
            skLineSegment(sketch, "E20.24.3", {"start": v(-63.01, -36.94) * mm, "end": v(-62.22, -37.93) * mm});
            skArc(sketch, "E20.25.0", {"start": v(-59.07, -35.13) * mm, "mid": v(-58.3, -35.45) * mm, "end": v(-57.49, -35.24) * mm});
            skArc(sketch, "E20.25.1", {"start": v(-57.49, -35.24) * mm, "mid": v(-57.4, -34.4) * mm, "end": v(-57.82, -33.69) * mm});
            skLineSegment(sketch, "E20.25.2", {"start": v(-58.78, -32.86) * mm, "end": v(-57.82, -33.69) * mm});
            skLineSegment(sketch, "E20.25.3", {"start": v(-60.03, -34.3) * mm, "end": v(-59.07, -35.13) * mm});
            skArc(sketch, "E20.26.0", {"start": v(-56.47, -31.81) * mm, "mid": v(-55.66, -31.99) * mm, "end": v(-54.9, -31.64) * mm});
            skArc(sketch, "E20.26.1", {"start": v(-54.9, -31.64) * mm, "mid": v(-54.96, -30.8) * mm, "end": v(-55.5, -30.17) * mm});
            skLineSegment(sketch, "E20.26.2", {"start": v(-56.6, -29.52) * mm, "end": v(-55.5, -30.17) * mm});
            skLineSegment(sketch, "E20.26.3", {"start": v(-57.57, -31.16) * mm, "end": v(-56.47, -31.81) * mm});
            skArc(sketch, "E20.27.0", {"start": v(-54.51, -28.08) * mm, "mid": v(-53.68, -28.11) * mm, "end": v(-53, -27.63) * mm});
            skArc(sketch, "E20.27.1", {"start": v(-53, -27.63) * mm, "mid": v(-53.2, -26.82) * mm, "end": v(-53.85, -26.3) * mm});
            skLineSegment(sketch, "E20.27.2", {"start": v(-55.04, -25.86) * mm, "end": v(-53.85, -26.3) * mm});
            skLineSegment(sketch, "E20.27.3", {"start": v(-55.7, -27.64) * mm, "end": v(-54.51, -28.08) * mm});
            skArc(sketch, "E20.28.0", {"start": v(-53.25, -24.07) * mm, "mid": v(-52.42, -23.94) * mm, "end": v(-51.83, -23.35) * mm});
            skArc(sketch, "E20.28.1", {"start": v(-51.83, -23.35) * mm, "mid": v(-52.18, -22.59) * mm, "end": v(-52.92, -22.19) * mm});
            skLineSegment(sketch, "E20.28.2", {"start": v(-54.17, -21.97) * mm, "end": v(-52.92, -22.19) * mm});
            skLineSegment(sketch, "E20.28.3", {"start": v(-54.5, -23.85) * mm, "end": v(-53.25, -24.07) * mm});
            skArc(sketch, "E20.29.0", {"start": v(-52.72, -19.89) * mm, "mid": v(-51.93, -19.62) * mm, "end": v(-51.46, -18.93) * mm});
            skArc(sketch, "E20.29.1", {"start": v(-51.46, -18.93) * mm, "mid": v(-51.94, -18.24) * mm, "end": v(-52.73, -17.98) * mm});
            skLineSegment(sketch, "E20.29.2", {"start": v(-54, -17.99) * mm, "end": v(-52.73, -17.98) * mm});
            skLineSegment(sketch, "E20.29.3", {"start": v(-54, -19.9) * mm, "end": v(-52.72, -19.89) * mm});
            skArc(sketch, "E20.30.0", {"start": v(-52.95, -15.68) * mm, "mid": v(-52.22, -15.28) * mm, "end": v(-51.88, -14.51) * mm});
            skArc(sketch, "E20.30.1", {"start": v(-51.88, -14.51) * mm, "mid": v(-52.47, -13.92) * mm, "end": v(-53.3, -13.8) * mm});
            skLineSegment(sketch, "E20.30.2", {"start": v(-54.55, -14.04) * mm, "end": v(-53.3, -13.8) * mm});
            skLineSegment(sketch, "E20.30.3", {"start": v(-54.2, -15.91) * mm, "end": v(-52.95, -15.68) * mm});
            skArc(sketch, "E20.31.0", {"start": v(-53.92, -11.58) * mm, "mid": v(-53.28, -11.05) * mm, "end": v(-53.08, -10.24) * mm});
            skArc(sketch, "E20.31.1", {"start": v(-53.08, -10.24) * mm, "mid": v(-53.77, -9.77) * mm, "end": v(-54.6, -9.8) * mm});
            skLineSegment(sketch, "E20.31.2", {"start": v(-55.79, -10.26) * mm, "end": v(-54.6, -9.8) * mm});
            skLineSegment(sketch, "E20.31.3", {"start": v(-55.11, -12.04) * mm, "end": v(-53.92, -11.58) * mm});
            skArc(sketch, "E20.32.0", {"start": v(-55.62, -7.73) * mm, "mid": v(-55.07, -7.09) * mm, "end": v(-55.02, -6.25) * mm});
            skArc(sketch, "E20.32.1", {"start": v(-55.02, -6.25) * mm, "mid": v(-55.78, -5.91) * mm, "end": v(-56.6, -6.1) * mm});
            skLineSegment(sketch, "E20.32.2", {"start": v(-57.69, -6.75) * mm, "end": v(-56.6, -6.1) * mm});
            skLineSegment(sketch, "E20.32.3", {"start": v(-56.7, -8.38) * mm, "end": v(-55.62, -7.73) * mm});
            skArc(sketch, "E20.33.0", {"start": v(-57.97, -4.23) * mm, "mid": v(-57.55, -3.5) * mm, "end": v(-57.65, -2.68) * mm});
            skArc(sketch, "E20.33.1", {"start": v(-57.65, -2.68) * mm, "mid": v(-58.46, -2.48) * mm, "end": v(-59.23, -2.8) * mm});
            skLineSegment(sketch, "E20.33.2", {"start": v(-60.18, -3.64) * mm, "end": v(-59.23, -2.8) * mm});
            skLineSegment(sketch, "E20.33.3", {"start": v(-58.92, -5.07) * mm, "end": v(-57.97, -4.23) * mm});
            skArc(sketch, "E20.34.0", {"start": v(-60.9, -1.22) * mm, "mid": v(-60.62, -0.43) * mm, "end": v(-60.87, 0.37) * mm});
            skArc(sketch, "E20.34.1", {"start": v(-60.87, 0.37) * mm, "mid": v(-61.7, 0.42) * mm, "end": v(-62.4, -0.03) * mm});
            skLineSegment(sketch, "E20.34.2", {"start": v(-63.19, -1.03) * mm, "end": v(-62.4, -0.03) * mm});
            skLineSegment(sketch, "E20.34.3", {"start": v(-61.7, -2.21) * mm, "end": v(-60.9, -1.22) * mm});
            skLineSegment(sketch, "E21.0", {"start": v(-65.77, 0.55) * mm, "end": v(-64.58, 2.8) * mm, "construction": true});
            skSolve(sketch);
        }
        {
            var Q0;
            Q0 = qSketchRegion(id + "F4", true);
            var Q1;
            Q1=makeQuery(id+"F4.imprint","IMPRINT",FACE,{"disambiguationData":[TD([[makeQuery(id+"F4.imprint","IMPRINT",EDGE,{"derivedFrom":sQuery(id+"F4.wireOp",EDGE,"E5.bottom")}),-1.0]])]});
            var Q2;
            Q2=makeQuery(id+"F4.imprint","IMPRINT",FACE,{"disambiguationData":[TD([[makeQuery(id+"F4.imprint","IMPRINT",EDGE,{"derivedFrom":sQuery(id+"F4.wireOp",EDGE,"E5.bottom")}),1.0]])]});
            var Q3;
            {var subQ6=sQuery(id+"F4.wireOp",EDGE,"E10.bottom");Q3=makeQuery(id+"F4.imprint","IMPRINT",FACE,{"disambiguationData":[TD([[makeQuery(id+"F4.imprint","IMPRINT",EDGE,{"derivedFrom":subQ6}),1.0]])]});}
            var Q4;
            {var subQ3=sQuery(id+"F4.wireOp",EDGE,"E12.1.0");var subQ4=sQuery(id+"F4.wireOp",EDGE,"E6");var subQ5=makeQuery(id+"F4.imprint","INTERSECT",VERTEX,{"derivedFrom":[subQ4,subQ3]});Q4=makeQuery(id+"F4.imprint","IMPRINT",FACE,{"disambiguationData":[TD([[makeQuery(id+"F4.imprint","IMPRINT",EDGE,{"disambiguationData":[TD([[subQ5,-1.0]])],"derivedFrom":subQ4}),1.0]])]});}
            var Q5;
            Q5=makeQuery(id+"F4.imprint","IMPRINT",FACE,{"disambiguationData":[TD([[makeQuery(id+"F4.imprint","IMPRINT",EDGE,{"derivedFrom":sQuery(id+"F4.wireOp",EDGE,"E12.1.14")}),1.0]])]});
            var Q6;
            {var subQ0=sQuery(id+"F4.wireOp",EDGE,"E12.1.29");Q6=makeQuery(id+"F4.imprint","IMPRINT",FACE,{"disambiguationData":[TD([[makeQuery(id+"F4.imprint","IMPRINT",EDGE,{"derivedFrom":subQ0}),-1.0]])]});}
            var Q7;
            Q7=makeQuery(id+"F4.imprint","IMPRINT",FACE,{"disambiguationData":[TD([[makeQuery(id+"F4.imprint","IMPRINT",EDGE,{"derivedFrom":sQuery(id+"F4.wireOp",EDGE,"E12.1.4")}),1.0]])]});
            var Q8;
            Q8=makeQuery(id+"F4.imprint","IMPRINT",FACE,{"disambiguationData":[TD([[makeQuery(id+"F4.imprint","IMPRINT",EDGE,{"derivedFrom":sQuery(id+"F4.wireOp",EDGE,"E12.1.19")}),1.0]])]});
            var Q9;
            Q9=makeQuery(id+"F4.imprint","IMPRINT",FACE,{"disambiguationData":[TD([[makeQuery(id+"F4.imprint","IMPRINT",EDGE,{"derivedFrom":sQuery(id+"F4.wireOp",EDGE,"E12.1.24")}),1.0]])]});
            var Q10;
            Q10=makeQuery(id+"F4.imprint","IMPRINT",FACE,{"disambiguationData":[TD([[makeQuery(id+"F4.imprint","IMPRINT",EDGE,{"derivedFrom":sQuery(id+"F4.wireOp",EDGE,"E10.top")}),1.0]])]});
            var Q11;
            {var subQ0=sQuery(id+"F4.wireOp",EDGE,"E11.0.1.3");Q11=makeQuery(id+"F4.imprint","IMPRINT",FACE,{"disambiguationData":[TD([[makeQuery(id+"F4.imprint","IMPRINT",EDGE,{"derivedFrom":subQ0}),1.0]])]});}
            var Q12;
            {var subQ0=sQuery(id+"F4.wireOp",EDGE,"E11.0.2.3");Q12=makeQuery(id+"F4.imprint","IMPRINT",FACE,{"disambiguationData":[TD([[makeQuery(id+"F4.imprint","IMPRINT",EDGE,{"derivedFrom":subQ0}),1.0]])]});}
            var Q13;
            {var subQ0=sQuery(id+"F4.wireOp",EDGE,"E11.0.3.3");Q13=makeQuery(id+"F4.imprint","IMPRINT",FACE,{"disambiguationData":[TD([[makeQuery(id+"F4.imprint","IMPRINT",EDGE,{"derivedFrom":subQ0}),1.0]])]});}
            var Q14;
            {var subQ0=sQuery(id+"F4.wireOp",EDGE,"E11.0.4.3");Q14=makeQuery(id+"F4.imprint","IMPRINT",FACE,{"disambiguationData":[TD([[makeQuery(id+"F4.imprint","IMPRINT",EDGE,{"derivedFrom":subQ0}),1.0]])]});}
            var Q15;
            {var subQ0=sQuery(id+"F4.wireOp",EDGE,"E11.0.5.3");Q15=makeQuery(id+"F4.imprint","IMPRINT",FACE,{"disambiguationData":[TD([[makeQuery(id+"F4.imprint","IMPRINT",EDGE,{"derivedFrom":subQ0}),1.0]])]});}
            var Q16;
            {var subQ0=sQuery(id+"F4.wireOp",EDGE,"E11.0.5.0");Q16=makeQuery(id+"F4.imprint","IMPRINT",FACE,{"disambiguationData":[TD([[makeQuery(id+"F4.imprint","IMPRINT",EDGE,{"derivedFrom":subQ0}),1.0]])]});}
            var Q17;
            {var subQ0=sQuery(id+"F4.wireOp",EDGE,"E11.0.4.0");Q17=makeQuery(id+"F4.imprint","IMPRINT",FACE,{"disambiguationData":[TD([[makeQuery(id+"F4.imprint","IMPRINT",EDGE,{"derivedFrom":subQ0}),1.0]])]});}
            var Q18;
            {var subQ0=sQuery(id+"F4.wireOp",EDGE,"E11.0.3.0");Q18=makeQuery(id+"F4.imprint","IMPRINT",FACE,{"disambiguationData":[TD([[makeQuery(id+"F4.imprint","IMPRINT",EDGE,{"derivedFrom":subQ0}),1.0]])]});}
            var Q19;
            {var subQ0=sQuery(id+"F4.wireOp",EDGE,"E11.0.2.0");Q19=makeQuery(id+"F4.imprint","IMPRINT",FACE,{"disambiguationData":[TD([[makeQuery(id+"F4.imprint","IMPRINT",EDGE,{"derivedFrom":subQ0}),1.0]])]});}
            var Q20;
            {var subQ0=sQuery(id+"F4.wireOp",EDGE,"E11.0.1.0");Q20=makeQuery(id+"F4.imprint","IMPRINT",FACE,{"disambiguationData":[TD([[makeQuery(id+"F4.imprint","IMPRINT",EDGE,{"derivedFrom":subQ0}),1.0]])]});}
            var Q21;
            Q21=makeQuery(id+"F4.imprint","IMPRINT",FACE,{"disambiguationData":[TD([[makeQuery(id+"F4.imprint","IMPRINT",EDGE,{"derivedFrom":sQuery(id+"F4.wireOp",EDGE,"E9.left")}),-1.0]])]});
            var Q22;
            {var subQ21=sQuery(id+"F4.wireOp",EDGE,"E12.3.9");Q22=makeQuery(id+"F4.imprint","IMPRINT",FACE,{"disambiguationData":[TD([[makeQuery(id+"F4.imprint","IMPRINT",EDGE,{"derivedFrom":subQ21}),1.0]])]});}
            var Q23;
            {var subQ0=sQuery(id+"F4.wireOp",EDGE,"E12.3.3");Q23=makeQuery(id+"F4.imprint","IMPRINT",FACE,{"disambiguationData":[TD([[makeQuery(id+"F4.imprint","IMPRINT",EDGE,{"derivedFrom":subQ0}),-1.0]])]});}
            var Q24;
            Q24=makeQuery(id+"F4.imprint","IMPRINT",FACE,{"disambiguationData":[TD([[makeQuery(id+"F4.imprint","IMPRINT",EDGE,{"derivedFrom":sQuery(id+"F4.wireOp",EDGE,"E12.3.12")}),-1.0]])]});
            var Q25;
            Q25=makeQuery(id+"F4.imprint","IMPRINT",FACE,{"disambiguationData":[TD([[makeQuery(id+"F4.imprint","IMPRINT",EDGE,{"derivedFrom":sQuery(id+"F4.wireOp",EDGE,"E12.3.15")}),-1.0]])]});
            var Q26;
            {var subQ0=sQuery(id+"F4.wireOp",EDGE,"E12.3.5");Q26=makeQuery(id+"F4.imprint","IMPRINT",FACE,{"disambiguationData":[TD([[makeQuery(id+"F4.imprint","IMPRINT",EDGE,{"derivedFrom":subQ0}),1.0]])]});}
            var Q27;
            {var subQ0=sQuery(id+"F4.wireOp",EDGE,"E12.3.2");Q27=makeQuery(id+"F4.imprint","IMPRINT",FACE,{"disambiguationData":[TD([[makeQuery(id+"F4.imprint","IMPRINT",EDGE,{"derivedFrom":subQ0}),-1.0]])]});}
            var Q28;
            Q28=makeQuery(id+"F4.imprint","IMPRINT",FACE,{"disambiguationData":[TD([[makeQuery(id+"F4.imprint","IMPRINT",EDGE,{"derivedFrom":sQuery(id+"F4.wireOp",EDGE,"E12.3.14")}),1.0]])]});
            var Q29;
            {var subQ0=sQuery(id+"F4.wireOp",EDGE,"E12.3.29");Q29=makeQuery(id+"F4.imprint","IMPRINT",FACE,{"disambiguationData":[TD([[makeQuery(id+"F4.imprint","IMPRINT",EDGE,{"derivedFrom":subQ0}),-1.0]])]});}
            var Q30;
            Q30=makeQuery(id+"F4.imprint","IMPRINT",FACE,{"disambiguationData":[TD([[makeQuery(id+"F4.imprint","IMPRINT",EDGE,{"derivedFrom":sQuery(id+"F4.wireOp",EDGE,"E12.3.4")}),1.0]])]});
            var Q31;
            Q31=makeQuery(id+"F4.imprint","IMPRINT",FACE,{"disambiguationData":[TD([[makeQuery(id+"F4.imprint","IMPRINT",EDGE,{"derivedFrom":sQuery(id+"F4.wireOp",EDGE,"E12.3.19")}),1.0]])]});
            var Q32;
            Q32=makeQuery(id+"F4.imprint","IMPRINT",FACE,{"disambiguationData":[TD([[makeQuery(id+"F4.imprint","IMPRINT",EDGE,{"derivedFrom":sQuery(id+"F4.wireOp",EDGE,"E12.3.24")}),1.0]])]});
            var Q33;
            Q33=makeQuery(id+"F4.imprint","IMPRINT",FACE,{"disambiguationData":[TD([[makeQuery(id+"F4.imprint","IMPRINT",EDGE,{"derivedFrom":sQuery(id+"F4.wireOp",EDGE,"E12.3.7")}),1.0]])]});
            var Q34;
            {var subQ0=sQuery(id+"F4.wireOp",EDGE,"E12.2.3");Q34=makeQuery(id+"F4.imprint","IMPRINT",FACE,{"disambiguationData":[TD([[makeQuery(id+"F4.imprint","IMPRINT",EDGE,{"derivedFrom":subQ0}),-1.0]])]});}
            var Q35;
            Q35=makeQuery(id+"F4.imprint","IMPRINT",FACE,{"disambiguationData":[TD([[makeQuery(id+"F4.imprint","IMPRINT",EDGE,{"derivedFrom":sQuery(id+"F4.wireOp",EDGE,"E12.2.12")}),-1.0]])]});
            var Q36;
            Q36=makeQuery(id+"F4.imprint","IMPRINT",FACE,{"disambiguationData":[TD([[makeQuery(id+"F4.imprint","IMPRINT",EDGE,{"derivedFrom":sQuery(id+"F4.wireOp",EDGE,"E12.2.15")}),-1.0]])]});
            var Q37;
            {var subQ0=sQuery(id+"F4.wireOp",EDGE,"E12.2.5");Q37=makeQuery(id+"F4.imprint","IMPRINT",FACE,{"disambiguationData":[TD([[makeQuery(id+"F4.imprint","IMPRINT",EDGE,{"derivedFrom":subQ0}),1.0]])]});}
            var Q38;
            {var subQ0=sQuery(id+"F4.wireOp",EDGE,"E12.2.2");Q38=makeQuery(id+"F4.imprint","IMPRINT",FACE,{"disambiguationData":[TD([[makeQuery(id+"F4.imprint","IMPRINT",EDGE,{"derivedFrom":subQ0}),-1.0]])]});}
            var Q39;
            {var subQ3=sQuery(id+"F4.wireOp",EDGE,"E12.2.0");var subQ4=sQuery(id+"F4.wireOp",EDGE,"E6");var subQ5=makeQuery(id+"F4.imprint","INTERSECT",VERTEX,{"derivedFrom":[subQ4,subQ3]});Q39=makeQuery(id+"F4.imprint","IMPRINT",FACE,{"disambiguationData":[TD([[makeQuery(id+"F4.imprint","IMPRINT",EDGE,{"disambiguationData":[TD([[subQ5,-1.0]])],"derivedFrom":subQ4}),1.0]])]});}
            var Q40;
            {var subQ6=sQuery(id+"F4.wireOp",EDGE,"E12.2.9");Q40=makeQuery(id+"F4.imprint","IMPRINT",FACE,{"disambiguationData":[TD([[makeQuery(id+"F4.imprint","IMPRINT",EDGE,{"derivedFrom":subQ6}),1.0]])]});}
            var Q41;
            Q41=makeQuery(id+"F4.imprint","IMPRINT",FACE,{"disambiguationData":[TD([[makeQuery(id+"F4.imprint","IMPRINT",EDGE,{"derivedFrom":sQuery(id+"F4.wireOp",EDGE,"E12.2.7")}),1.0]])]});
            var Q42;
            Q42=makeQuery(id+"F4.imprint","IMPRINT",FACE,{"disambiguationData":[TD([[makeQuery(id+"F4.imprint","IMPRINT",EDGE,{"derivedFrom":sQuery(id+"F4.wireOp",EDGE,"E12.2.24")}),1.0]])]});
            var Q43;
            Q43=makeQuery(id+"F4.imprint","IMPRINT",FACE,{"disambiguationData":[TD([[makeQuery(id+"F4.imprint","IMPRINT",EDGE,{"derivedFrom":sQuery(id+"F4.wireOp",EDGE,"E12.2.19")}),1.0]])]});
            var Q44;
            Q44=makeQuery(id+"F4.imprint","IMPRINT",FACE,{"disambiguationData":[TD([[makeQuery(id+"F4.imprint","IMPRINT",EDGE,{"derivedFrom":sQuery(id+"F4.wireOp",EDGE,"E12.2.4")}),1.0]])]});
            var Q45;
            {var subQ0=sQuery(id+"F4.wireOp",EDGE,"E12.2.29");Q45=makeQuery(id+"F4.imprint","IMPRINT",FACE,{"disambiguationData":[TD([[makeQuery(id+"F4.imprint","IMPRINT",EDGE,{"derivedFrom":subQ0}),-1.0]])]});}
            var Q46;
            Q46=makeQuery(id+"F4.imprint","IMPRINT",FACE,{"disambiguationData":[TD([[makeQuery(id+"F4.imprint","IMPRINT",EDGE,{"derivedFrom":sQuery(id+"F4.wireOp",EDGE,"E12.2.14")}),1.0]])]});
            var Q47;
            {var subQ0=sQuery(id+"F4.wireOp",EDGE,"E12.1.3");Q47=makeQuery(id+"F4.imprint","IMPRINT",FACE,{"disambiguationData":[TD([[makeQuery(id+"F4.imprint","IMPRINT",EDGE,{"derivedFrom":subQ0}),-1.0]])]});}
            var Q48;
            Q48=makeQuery(id+"F4.imprint","IMPRINT",FACE,{"disambiguationData":[TD([[makeQuery(id+"F4.imprint","IMPRINT",EDGE,{"derivedFrom":sQuery(id+"F4.wireOp",EDGE,"E12.1.12")}),-1.0]])]});
            var Q49;
            Q49=makeQuery(id+"F4.imprint","IMPRINT",FACE,{"disambiguationData":[TD([[makeQuery(id+"F4.imprint","IMPRINT",EDGE,{"derivedFrom":sQuery(id+"F4.wireOp",EDGE,"E12.1.15")}),-1.0]])]});
            var Q50;
            {var subQ0=sQuery(id+"F4.wireOp",EDGE,"E12.1.5");Q50=makeQuery(id+"F4.imprint","IMPRINT",FACE,{"disambiguationData":[TD([[makeQuery(id+"F4.imprint","IMPRINT",EDGE,{"derivedFrom":subQ0}),1.0]])]});}
            var Q51;
            {var subQ0=sQuery(id+"F4.wireOp",EDGE,"E12.1.2");Q51=makeQuery(id+"F4.imprint","IMPRINT",FACE,{"disambiguationData":[TD([[makeQuery(id+"F4.imprint","IMPRINT",EDGE,{"derivedFrom":subQ0}),-1.0]])]});}
            var Q52;
            {var subQ5=sQuery(id+"F4.wireOp",EDGE,"E12.2.20");Q52=makeQuery(id+"F4.imprint","IMPRINT",FACE,{"disambiguationData":[TD([[makeQuery(id+"F4.imprint","IMPRINT",EDGE,{"derivedFrom":subQ5}),-1.0]])]});}
            var Q53;
            {var subQ5=sQuery(id+"F4.wireOp",EDGE,"E12.1.20");Q53=makeQuery(id+"F4.imprint","IMPRINT",FACE,{"disambiguationData":[TD([[makeQuery(id+"F4.imprint","IMPRINT",EDGE,{"derivedFrom":subQ5}),-1.0]])]});}
            extrude(context, id + "F5", {"entities" : qUnion([Q0, Q1, Q2, Q3, Q4, Q5, Q6, Q7, Q8, Q9, Q10, Q11, Q12, Q13, Q14, Q15, Q16, Q17, Q18, Q19, Q20, Q21, Q22, Q23, Q24, Q25, Q26, Q27, Q28, Q29, Q30, Q31, Q32, Q33, Q34, Q35, Q36, Q37, Q38, Q39, Q40, Q41, Q42, Q43, Q44, Q45, Q46, Q47, Q48, Q49, Q50, Q51, Q52, Q53]), "operationType" : NewBodyOperationType.ADD, "endBound" : BoundingType.SYMMETRIC, "depth" : 5.08 * mm, "offsetDistance" : 25.4 * mm});
        }
        {
            var Q0;
            {var subQ18=sQuery(id+"F4.wireOp",EDGE,"E11.0.1.0");var subQ27=sQuery(id+"F0.wireOp",EDGE,"E0.left");var subQ28=sQuery(id+"F0.wireOp",EDGE,"E0.top");var subQ29=sQuery(id+"F0.wireOp",EDGE,"E0.right");var subQ30=sQuery(id+"F0.wireOp",EDGE,"E0.bottom");Q0=makeQuery(id+"F5.boolean.opBoolean","SPLIT",FACE,{"disambiguationData":[TD([makeQuery(id+"F5.opExtrude","SWEPT_FACE",FACE,{"disambiguationData":[OSD([subQ18])]})])],"derivedFrom":makeQuery(id+"F3.boolean.opBoolean","SPLIT",FACE,{"disambiguationData":[TD([makeQuery(id+"F1.opExtrude","SWEPT_FACE",FACE,{"disambiguationData":[OSD([subQ30])]})])],"derivedFrom":makeQuery(id+"F1.opExtrude","CAP_FACE",FACE,{"disambiguationData":[OSD([subQ30,subQ28,subQ27,subQ29])],"isStart":false})})});}
            var Q1;
            {var subQ7=sQuery(id+"F4.wireOp",EDGE,"E11.0.1.3");var subQ13=sQuery(id+"F0.wireOp",EDGE,"E0.right");var subQ27=sQuery(id+"F0.wireOp",EDGE,"E0.left");var subQ28=sQuery(id+"F0.wireOp",EDGE,"E0.top");var subQ29=sQuery(id+"F0.wireOp",EDGE,"E0.bottom");Q1=makeQuery(id+"F5.boolean.opBoolean","SPLIT",FACE,{"disambiguationData":[TD([makeQuery(id+"F5.opExtrude","SWEPT_FACE",FACE,{"disambiguationData":[OSD([subQ7])]})])],"derivedFrom":makeQuery(id+"F3.boolean.opBoolean","SPLIT",FACE,{"disambiguationData":[TD([makeQuery(id+"F1.opExtrude","SWEPT_FACE",FACE,{"disambiguationData":[OSD([subQ29])]})])],"derivedFrom":makeQuery(id+"F1.opExtrude","CAP_FACE",FACE,{"disambiguationData":[OSD([subQ29,subQ28,subQ27,subQ13])],"isStart":false})})});}
            var Q2;
            {var subQ1=sQuery(id+"F4.wireOp",EDGE,"E12.1.3");var subQ3=sQuery(id+"F0.wireOp",EDGE,"E0.top");var subQ14=sQuery(id+"F0.wireOp",EDGE,"E0.right");var subQ22=sQuery(id+"F0.wireOp",EDGE,"E0.left");var subQ23=sQuery(id+"F0.wireOp",EDGE,"E0.bottom");Q2=makeQuery(id+"F5.boolean.opBoolean","SPLIT",FACE,{"disambiguationData":[TD([makeQuery(id+"F5.opExtrude","SWEPT_FACE",FACE,{"disambiguationData":[OSD([subQ1])]})])],"derivedFrom":makeQuery(id+"F3.boolean.opBoolean","SPLIT",FACE,{"disambiguationData":[TD([makeQuery(id+"F1.opExtrude","SWEPT_FACE",FACE,{"disambiguationData":[OSD([subQ23])]})])],"derivedFrom":makeQuery(id+"F1.opExtrude","CAP_FACE",FACE,{"disambiguationData":[OSD([subQ23,subQ3,subQ22,subQ14])],"isStart":false})})});}
            var Q3;
            {var subQ14=sQuery(id+"F0.wireOp",EDGE,"E0.top");var subQ20=sQuery(id+"F4.wireOp",EDGE,"E12.2.3");var subQ27=sQuery(id+"F0.wireOp",EDGE,"E0.left");var subQ28=sQuery(id+"F0.wireOp",EDGE,"E0.right");var subQ29=sQuery(id+"F0.wireOp",EDGE,"E0.bottom");Q3=makeQuery(id+"F5.boolean.opBoolean","SPLIT",FACE,{"disambiguationData":[TD([makeQuery(id+"F5.opExtrude","SWEPT_FACE",FACE,{"disambiguationData":[OSD([subQ20])]})])],"derivedFrom":makeQuery(id+"F3.boolean.opBoolean","SPLIT",FACE,{"disambiguationData":[TD([makeQuery(id+"F1.opExtrude","SWEPT_FACE",FACE,{"disambiguationData":[OSD([subQ29])]})])],"derivedFrom":makeQuery(id+"F1.opExtrude","CAP_FACE",FACE,{"disambiguationData":[OSD([subQ29,subQ14,subQ27,subQ28])],"isStart":false})})});}
            var Q4;
            {var subQ0=sQuery(id+"F0.wireOp",EDGE,"E0.top");var subQ4=sQuery(id+"F4.wireOp",EDGE,"E12.2.17");var subQ5=sQuery(id+"F0.wireOp",EDGE,"E0.left");var subQ6=sQuery(id+"F0.wireOp",EDGE,"E0.right");var subQ7=sQuery(id+"F0.wireOp",EDGE,"E0.bottom");Q4=makeQuery(id+"F5.boolean.opBoolean","SPLIT",FACE,{"disambiguationData":[TD([makeQuery(id+"F5.opExtrude","SWEPT_FACE",FACE,{"disambiguationData":[OSD([subQ4])]})])],"derivedFrom":makeQuery(id+"F3.boolean.opBoolean","SPLIT",FACE,{"disambiguationData":[TD([makeQuery(id+"F1.opExtrude","SWEPT_FACE",FACE,{"disambiguationData":[OSD([subQ7])]})])],"derivedFrom":makeQuery(id+"F1.opExtrude","CAP_FACE",FACE,{"disambiguationData":[OSD([subQ7,subQ0,subQ5,subQ6])],"isStart":false})})});}
            var Q5;
            {var subQ0=sQuery(id+"F0.wireOp",EDGE,"E0.right");var subQ4=sQuery(id+"F4.wireOp",EDGE,"E12.1.17");var subQ5=sQuery(id+"F0.wireOp",EDGE,"E0.left");var subQ6=sQuery(id+"F0.wireOp",EDGE,"E0.top");var subQ7=sQuery(id+"F0.wireOp",EDGE,"E0.bottom");Q5=makeQuery(id+"F5.boolean.opBoolean","SPLIT",FACE,{"disambiguationData":[TD([makeQuery(id+"F5.opExtrude","SWEPT_FACE",FACE,{"disambiguationData":[OSD([subQ4])]})])],"derivedFrom":makeQuery(id+"F3.boolean.opBoolean","SPLIT",FACE,{"disambiguationData":[TD([makeQuery(id+"F1.opExtrude","SWEPT_FACE",FACE,{"disambiguationData":[OSD([subQ7])]})])],"derivedFrom":makeQuery(id+"F1.opExtrude","CAP_FACE",FACE,{"disambiguationData":[OSD([subQ7,subQ6,subQ5,subQ0])],"isStart":false})})});}
            extrude(context, id + "F6", {"entities" : qUnion([Q0, Q1, Q2, Q3, Q4, Q5]), "operationType" : NewBodyOperationType.REMOVE, "endBound" : BoundingType.UP_TO_NEXT, "oppositeDirection" : true, "depth" : 25.4 * mm, "offsetDistance" : 25.4 * mm});
        }
        {
            var Q0;
            {var subQ114=sQuery(id+"F0.wireOp",EDGE,"E0.bottom");var subQ115=makeQuery(id+"F1.opExtrude","SWEPT_FACE",FACE,{"disambiguationData":[OSD([subQ114])]});var subQ119=sQuery(id+"F0.wireOp",EDGE,"E0.right");var subQ127=sQuery(id+"F0.wireOp",EDGE,"E0.top");var subQ133=sQuery(id+"F0.wireOp",EDGE,"E0.left");Q0=makeQuery(id+"F5.boolean.opBoolean","SPLIT",FACE,{"disambiguationData":[TD([subQ115])],"derivedFrom":makeQuery(id+"F3.boolean.opBoolean","SPLIT",FACE,{"disambiguationData":[TD([subQ115])],"derivedFrom":makeQuery(id+"F1.opExtrude","CAP_FACE",FACE,{"disambiguationData":[OSD([subQ114,subQ127,subQ133,subQ119])],"isStart":false})})});}
            var sketch = newSketch(context, id + "F7", { "sketchPlane" : qUnion([Q0])});
            skCircle(sketch, "E22", {"center": v(-56.9, 16.74) * mm, "radius": 12.7 * mm});
            skCircle(sketch, "E23", {"center": v(-56.9, 16.74) * mm, "radius": 10.16 * mm});
            skCircle(sketch, "E24", {"center": v(-56.9, 16.74) * mm, "radius": 5.08 * mm});
            skCircle(sketch, "E25", {"center": v(-56.9, 16.74) * mm, "radius": 2.54 * mm});
            skSolve(sketch);
        }
        {
            var Q0;
            Q0=makeQuery(id+"F7.imprint","IMPRINT",FACE,{"disambiguationData":[TD([[makeQuery(id+"F7.imprint","IMPRINT",EDGE,{"derivedFrom":sQuery(id+"F7.wireOp",EDGE,"E22")}),1.0]])]});
            var Q1;
            Q1=makeQuery(id+"F7.imprint","IMPRINT",FACE,{"disambiguationData":[TD([[makeQuery(id+"F7.imprint","IMPRINT",EDGE,{"derivedFrom":sQuery(id+"F7.wireOp",EDGE,"E24")}),1.0]])]});
            extrude(context, id + "F8", {"entities" : qUnion([Q0, Q1]), "operationType" : NewBodyOperationType.ADD, "depth" : 2.54 * mm, "offsetDistance" : 25.4 * mm});
        }
        {
            var Q0;
            {var subQ114=sQuery(id+"F0.wireOp",EDGE,"E0.bottom");var subQ115=makeQuery(id+"F1.opExtrude","SWEPT_FACE",FACE,{"disambiguationData":[OSD([subQ114])]});var subQ119=sQuery(id+"F0.wireOp",EDGE,"E0.right");var subQ127=sQuery(id+"F0.wireOp",EDGE,"E0.top");var subQ133=sQuery(id+"F0.wireOp",EDGE,"E0.left");Q0=makeQuery(id+"Fo6Mcm9j0ZxEgct_1.boolean.opBoolean","SPLIT",FACE,{"disambiguationData":[OD(0.0)],"derivedFrom":makeQuery(id+"F8.boolean.opBoolean","SPLIT",FACE,{"disambiguationData":[TD([makeQuery(id+"F8.opExtrude","SWEPT_FACE",FACE,{"disambiguationData":[OSD([sQuery(id+"F7.wireOp",EDGE,"E23")])]})])],"derivedFrom":makeQuery(id+"F5.boolean.opBoolean","SPLIT",FACE,{"disambiguationData":[TD([subQ115])],"derivedFrom":makeQuery(id+"F3.boolean.opBoolean","SPLIT",FACE,{"disambiguationData":[TD([subQ115])],"derivedFrom":makeQuery(id+"F1.opExtrude","CAP_FACE",FACE,{"disambiguationData":[OSD([subQ114,subQ127,subQ133,subQ119])],"isStart":false})})})})});}
            var sketch = newSketch(context, id + "F9", { "sketchPlane" : qUnion([Q0])});
            skPoint(sketch, "E26", {"position": v(-56.9, 16.74) * mm});
            skCircle(sketch, "E27", {"center": v(-49.29, 16.74) * mm, "radius": 2.54 * mm});
            skLineSegment(sketch, "E28", {"start": v(-46.75, 16.74) * mm, "end": v(-51.83, 16.74) * mm});
            skSolve(sketch);
        }
        {
            var Q0;
            {var subQ0=sQuery(id+"F9.wireOp",EDGE,"E28");Q0=makeQuery(id+"F9.imprint","IMPRINT",FACE,{"disambiguationData":[TD([[makeQuery(id+"F9.imprint","IMPRINT",EDGE,{"derivedFrom":subQ0}),-1.0]])]});}
            var Q1;
            Q1=sQuery(id+"F9.wireOp",EDGE,"E28");
            revolve(context, id + "F10", {"entities" : qUnion([Q0]), "axis" : qUnion([Q1]), "revolveType" : RevolveType.ONE_DIRECTION, "oppositeDirection" : true, "angle" : 180 * degree});
        }
        {
            var Q0;
            Q0=makeQuery(id+"F10.opRevolve","SWEPT_BODY",BODY,{"disambiguationData":[OSD([sQuery(id+"F9.wireOp",EDGE,"E27"),sQuery(id+"F9.wireOp",EDGE,"E28")])]});
            var Q1;
            Q1=makeQuery(id+"F8.opExtrude","SWEPT_FACE",FACE,{"disambiguationData":[OSD([sQuery(id+"F7.wireOp",EDGE,"E25")])]});
            circularPattern(context, id + "F11", {"entities" : qUnion([Q0]), "axis" : qUnion([Q1]), "angle" : 360 * degree, "instanceCount" : 8, "equalSpace" : true});
        }
        {
            var Q0;
            {var subQ114=sQuery(id+"F0.wireOp",EDGE,"E0.bottom");var subQ115=makeQuery(id+"F1.opExtrude","SWEPT_FACE",FACE,{"disambiguationData":[OSD([subQ114])]});var subQ119=sQuery(id+"F0.wireOp",EDGE,"E0.right");var subQ127=sQuery(id+"F0.wireOp",EDGE,"E0.top");var subQ133=sQuery(id+"F0.wireOp",EDGE,"E0.left");Q0=makeQuery(id+"F8.boolean.opBoolean","SPLIT",FACE,{"disambiguationData":[TD([makeQuery(id+"F8.opExtrude","SWEPT_FACE",FACE,{"disambiguationData":[OSD([sQuery(id+"F7.wireOp",EDGE,"E25")])]})])],"derivedFrom":makeQuery(id+"F5.boolean.opBoolean","SPLIT",FACE,{"disambiguationData":[TD([subQ115])],"derivedFrom":makeQuery(id+"F3.boolean.opBoolean","SPLIT",FACE,{"disambiguationData":[TD([subQ115])],"derivedFrom":makeQuery(id+"F1.opExtrude","CAP_FACE",FACE,{"disambiguationData":[OSD([subQ114,subQ127,subQ133,subQ119])],"isStart":false})})})});}
            extrude(context, id + "F12", {"entities" : qUnion([Q0]), "operationType" : NewBodyOperationType.REMOVE, "endBound" : BoundingType.UP_TO_NEXT, "oppositeDirection" : true, "depth" : 25.4 * mm, "offsetDistance" : 25.4 * mm});
        }
        {
            var Q0;
            {var subQ156=sQuery(id+"F0.wireOp",EDGE,"E0.bottom");var subQ157=makeQuery(id+"F1.opExtrude","SWEPT_FACE",FACE,{"disambiguationData":[OSD([subQ156])]});var subQ161=sQuery(id+"F0.wireOp",EDGE,"E0.right");var subQ169=sQuery(id+"F0.wireOp",EDGE,"E0.top");var subQ175=sQuery(id+"F0.wireOp",EDGE,"E0.left");Q0=makeQuery(id+"F8.boolean.opBoolean","SPLIT",FACE,{"disambiguationData":[TD([subQ157])],"derivedFrom":makeQuery(id+"F5.boolean.opBoolean","SPLIT",FACE,{"disambiguationData":[TD([subQ157])],"derivedFrom":makeQuery(id+"F3.boolean.opBoolean","SPLIT",FACE,{"disambiguationData":[TD([subQ157])],"derivedFrom":makeQuery(id+"F1.opExtrude","CAP_FACE",FACE,{"disambiguationData":[OSD([subQ156,subQ169,subQ175,subQ161])],"isStart":false})})})});}
            var sketch = newSketch(context, id + "F13", { "sketchPlane" : qUnion([Q0])});
            skCircle(sketch, "E29", {"center": v(64.51, 17.38) * mm, "radius": 5.08 * mm});
            skLineSegment(sketch, "E30", {"start": v(64.51, 17.38) * mm, "end": v(62.9, 12.56) * mm});
            skLineSegment(sketch, "E31", {"start": v(64.51, 17.38) * mm, "end": v(64.65, 12.3) * mm});
            skLineSegment(sketch, "E32", {"start": v(64.51, 17.38) * mm, "end": v(65.53, 12.4) * mm});
            skLineSegment(sketch, "E33", {"start": v(64.51, 17.38) * mm, "end": v(67.17, 13.04) * mm});
            skLineSegment(sketch, "E34", {"start": v(65.53, 12.4) * mm, "end": v(74.84, -11.23) * mm});
            skLineSegment(sketch, "E35", {"start": v(67.17, 13.04) * mm, "end": v(76.48, -10.59) * mm});
            skLineSegment(sketch, "E36", {"start": v(64.65, 12.3) * mm, "end": v(65.53, 12.4) * mm});
            skLineSegment(sketch, "E37", {"start": v(64.65, 12.3) * mm, "end": v(60.9, -12.82) * mm});
            skLineSegment(sketch, "E38", {"start": v(62.9, 12.56) * mm, "end": v(59.15, -12.56) * mm});
            skLineSegment(sketch, "E39", {"start": v(59.15, -12.56) * mm, "end": v(60.9, -12.82) * mm});
            skLineSegment(sketch, "E40", {"start": v(74.84, -11.23) * mm, "end": v(76.48, -10.59) * mm});
            skLineSegment(sketch, "E41", {"start": v(64.51, 17.38) * mm, "end": v(63.76, 12.35) * mm});
            skLineSegment(sketch, "E42", {"start": v(64.51, 17.38) * mm, "end": v(66.37, 12.65) * mm});
            skCircle(sketch, "E43", {"center": v(64.51, 17.38) * mm, "radius": 3.81 * mm});
            skSolve(sketch);
        }
        {
            var Q0;
            {var subQ1=sQuery(id+"F13.wireOp",EDGE,"E29");var subQ3=sQuery(id+"F13.wireOp",EDGE,"E41");var subQ4=makeQuery(id+"F13.imprint","INTERSECT",VERTEX,{"derivedFrom":[subQ1,subQ3]});Q0=makeQuery(id+"F13.imprint","IMPRINT",FACE,{"disambiguationData":[TD([[makeQuery(id+"F13.imprint","IMPRINT",EDGE,{"disambiguationData":[TD([[subQ4,1.0]])],"derivedFrom":subQ3}),1.0]])]});}
            var Q1;
            {var subQ1=sQuery(id+"F13.wireOp",EDGE,"E29");var subQ3=sQuery(id+"F13.wireOp",EDGE,"E41");var subQ4=makeQuery(id+"F13.imprint","INTERSECT",VERTEX,{"derivedFrom":[subQ1,subQ3]});Q1=makeQuery(id+"F13.imprint","IMPRINT",FACE,{"disambiguationData":[TD([[makeQuery(id+"F13.imprint","IMPRINT",EDGE,{"disambiguationData":[TD([[subQ4,1.0]])],"derivedFrom":subQ3}),-1.0]])]});}
            var Q2;
            {var subQ0=sQuery(id+"F13.wireOp",EDGE,"E36");Q2=makeQuery(id+"F13.imprint","IMPRINT",FACE,{"disambiguationData":[TD([[makeQuery(id+"F13.imprint","IMPRINT",EDGE,{"derivedFrom":subQ0}),1.0]])]});}
            var Q3;
            {var subQ1=sQuery(id+"F13.wireOp",EDGE,"E29");var subQ3=sQuery(id+"F13.wireOp",EDGE,"E42");var subQ4=makeQuery(id+"F13.imprint","INTERSECT",VERTEX,{"derivedFrom":[subQ1,subQ3]});Q3=makeQuery(id+"F13.imprint","IMPRINT",FACE,{"disambiguationData":[TD([[makeQuery(id+"F13.imprint","IMPRINT",EDGE,{"disambiguationData":[TD([[subQ4,1.0]])],"derivedFrom":subQ3}),-1.0]])]});}
            var Q4;
            {var subQ1=sQuery(id+"F13.wireOp",EDGE,"E29");var subQ3=sQuery(id+"F13.wireOp",EDGE,"E42");var subQ4=makeQuery(id+"F13.imprint","INTERSECT",VERTEX,{"derivedFrom":[subQ1,subQ3]});Q4=makeQuery(id+"F13.imprint","IMPRINT",FACE,{"disambiguationData":[TD([[makeQuery(id+"F13.imprint","IMPRINT",EDGE,{"disambiguationData":[TD([[subQ4,1.0]])],"derivedFrom":subQ3}),1.0]])]});}
            var Q5;
            {var subQ3=sQuery(id+"F13.wireOp",EDGE,"E34");Q5=makeQuery(id+"F13.imprint","IMPRINT",FACE,{"disambiguationData":[TD([[makeQuery(id+"F13.imprint","IMPRINT",EDGE,{"derivedFrom":subQ3}),1.0]])]});}
            var Q6;
            {var subQ1=sQuery(id+"F13.wireOp",EDGE,"E37");Q6=makeQuery(id+"F13.imprint","IMPRINT",FACE,{"disambiguationData":[TD([[makeQuery(id+"F13.imprint","IMPRINT",EDGE,{"derivedFrom":subQ1}),-1.0]])]});}
            var Q7;
            {var subQ0=sQuery(id+"F13.wireOp",EDGE,"E30");var subQ5=sQuery(id+"F13.wireOp",EDGE,"E43");var subQ6=makeQuery(id+"F13.imprint","INTERSECT",VERTEX,{"derivedFrom":[subQ0,subQ5]});Q7=makeQuery(id+"F13.imprint","IMPRINT",FACE,{"disambiguationData":[TD([[makeQuery(id+"F13.imprint","IMPRINT",EDGE,{"disambiguationData":[TD([[subQ6,1.0]])],"derivedFrom":subQ5}),-1.0]])]});}
            extrude(context, id + "F14", {"entities" : qUnion([Q0, Q1, Q2, Q3, Q4, Q5, Q6, Q7]), "operationType" : NewBodyOperationType.ADD, "depth" : 2.54 * mm, "offsetDistance" : 25.4 * mm});
        }
        {
            var Q0;
            {var subQ156=sQuery(id+"F0.wireOp",EDGE,"E0.bottom");var subQ157=makeQuery(id+"F1.opExtrude","SWEPT_FACE",FACE,{"disambiguationData":[OSD([subQ156])]});var subQ161=sQuery(id+"F0.wireOp",EDGE,"E0.right");var subQ169=sQuery(id+"F0.wireOp",EDGE,"E0.top");var subQ175=sQuery(id+"F0.wireOp",EDGE,"E0.left");Q0=makeQuery(id+"F14.boolean.opBoolean","SPLIT",FACE,{"disambiguationData":[TD([subQ157])],"derivedFrom":makeQuery(id+"F8.boolean.opBoolean","SPLIT",FACE,{"disambiguationData":[TD([subQ157])],"derivedFrom":makeQuery(id+"F5.boolean.opBoolean","SPLIT",FACE,{"disambiguationData":[TD([subQ157])],"derivedFrom":makeQuery(id+"F3.boolean.opBoolean","SPLIT",FACE,{"disambiguationData":[TD([subQ157])],"derivedFrom":makeQuery(id+"F1.opExtrude","CAP_FACE",FACE,{"disambiguationData":[OSD([subQ156,subQ169,subQ175,subQ161])],"isStart":false})})})})});}
            var sketch = newSketch(context, id + "F15", { "sketchPlane" : qUnion([Q0])});
            skLineSegment(sketch, "E44", {"start": v(62.77, -0.26) * mm, "end": v(70.18, 0.58) * mm});
            skLineSegment(sketch, "E45", {"start": v(56.32, -0.49) * mm, "end": v(76.51, 1.81) * mm});
            skLineSegment(sketch, "E46", {"start": v(56.44, -1.5) * mm, "end": v(76.63, 0.8) * mm});
            skLineSegment(sketch, "E47", {"start": v(66.42, 0.66) * mm, "end": v(66.47, 0.16) * mm});
            skLineSegment(sketch, "E48", {"start": v(66.47, 0.16) * mm, "end": v(66.53, -0.35) * mm});
            skLineSegment(sketch, "E49", {"start": v(56.32, -0.49) * mm, "end": v(56.44, -1.5) * mm});
            skLineSegment(sketch, "E50", {"start": v(76.51, 1.81) * mm, "end": v(76.63, 0.8) * mm});
            skLineSegment(sketch, "E51", {"start": v(56.38, -1) * mm, "end": v(62.77, -0.26) * mm});
            skLineSegment(sketch, "E52", {"start": v(76.57, 1.31) * mm, "end": v(70.18, 0.58) * mm});
            skLineSegment(sketch, "E53", {"start": v(65.91, 0.6) * mm, "end": v(65.55, 3.76) * mm});
            skLineSegment(sketch, "E54", {"start": v(66.92, 0.72) * mm, "end": v(66.56, 3.88) * mm});
            skLineSegment(sketch, "E55", {"start": v(66.56, 3.88) * mm, "end": v(65.55, 3.76) * mm});
            skSolve(sketch);
        }
        {
            var Q0;
            {var subQ0=sQuery(id+"F15.wireOp",EDGE,"E49");var subQ1=sQuery(id+"F15.wireOp",EDGE,"E45");var subQ2=makeQuery(id+"F15.imprint","INTERSECT",VERTEX,{"derivedFrom":[subQ1,subQ0]});Q0=makeQuery(id+"F15.imprint","IMPRINT",FACE,{"disambiguationData":[TD([[makeQuery(id+"F15.imprint","IMPRINT",EDGE,{"disambiguationData":[TD([[subQ2,-1.0]])],"derivedFrom":subQ1}),-1.0]])]});}
            var Q1;
            {var subQ3=sQuery(id+"F15.wireOp",EDGE,"E48");Q1=makeQuery(id+"F15.imprint","IMPRINT",FACE,{"disambiguationData":[TD([[makeQuery(id+"F15.imprint","IMPRINT",EDGE,{"derivedFrom":subQ3}),-1.0]])]});}
            var Q2;
            {var subQ3=sQuery(id+"F15.wireOp",EDGE,"E48");Q2=makeQuery(id+"F15.imprint","IMPRINT",FACE,{"disambiguationData":[TD([[makeQuery(id+"F15.imprint","IMPRINT",EDGE,{"derivedFrom":subQ3}),1.0]])]});}
            var Q3;
            {var subQ0=sQuery(id+"F15.wireOp",EDGE,"E50");var subQ1=sQuery(id+"F15.wireOp",EDGE,"E45");var subQ2=makeQuery(id+"F15.imprint","INTERSECT",VERTEX,{"derivedFrom":[subQ1,subQ0]});Q3=makeQuery(id+"F15.imprint","IMPRINT",FACE,{"disambiguationData":[TD([[makeQuery(id+"F15.imprint","IMPRINT",EDGE,{"disambiguationData":[TD([[subQ2,1.0]])],"derivedFrom":subQ1}),-1.0]])]});}
            var Q4;
            {var subQ3=sQuery(id+"F15.wireOp",EDGE,"E53");Q4=makeQuery(id+"F15.imprint","IMPRINT",FACE,{"disambiguationData":[TD([[makeQuery(id+"F15.imprint","IMPRINT",EDGE,{"derivedFrom":subQ3}),-1.0]])]});}
            var Q5;
            Q5=sQuery(id+"F15.wireOp",EDGE,"E44");
            revolve(context, id + "F16", {"entities" : qUnion([Q0, Q1, Q2, Q3, Q4]), "axis" : qUnion([Q5]), "revolveType" : RevolveType.FULL});
        }
        {
            var Q0;
            {var subQ156=sQuery(id+"F0.wireOp",EDGE,"E0.bottom");var subQ157=makeQuery(id+"F1.opExtrude","SWEPT_FACE",FACE,{"disambiguationData":[OSD([subQ156])]});var subQ161=sQuery(id+"F0.wireOp",EDGE,"E0.right");var subQ169=sQuery(id+"F0.wireOp",EDGE,"E0.top");var subQ175=sQuery(id+"F0.wireOp",EDGE,"E0.left");Q0=makeQuery(id+"F14.boolean.opBoolean","SPLIT",FACE,{"disambiguationData":[TD([subQ157])],"derivedFrom":makeQuery(id+"F8.boolean.opBoolean","SPLIT",FACE,{"disambiguationData":[TD([subQ157])],"derivedFrom":makeQuery(id+"F5.boolean.opBoolean","SPLIT",FACE,{"disambiguationData":[TD([subQ157])],"derivedFrom":makeQuery(id+"F3.boolean.opBoolean","SPLIT",FACE,{"disambiguationData":[TD([subQ157])],"derivedFrom":makeQuery(id+"F1.opExtrude","CAP_FACE",FACE,{"disambiguationData":[OSD([subQ156,subQ169,subQ175,subQ161])],"isStart":false})})})})});}
            var sketch = newSketch(context, id + "F17", { "sketchPlane" : qUnion([Q0])});
            skPoint(sketch, "E56", {"position": v(64.51, 17.38) * mm});
            skLineSegment(sketch, "E57", {"start": v(64.51, 17.38) * mm, "end": v(63.94, 22.42) * mm});
            skLineSegment(sketch, "E58", {"start": v(62.94, 22.2) * mm, "end": v(62.37, 27.24) * mm});
            skLineSegment(sketch, "E59", {"start": v(65.03, 22.43) * mm, "end": v(64.45, 27.48) * mm});
            skLineSegment(sketch, "E60", {"start": v(62.37, 27.24) * mm, "end": v(64.45, 27.48) * mm});
            skLineSegment(sketch, "E61", {"start": v(63.4, 27.36) * mm, "end": v(63.94, 22.42) * mm});
            skLineSegment(sketch, "E62", {"start": v(62.65, 27.27) * mm, "end": v(62.94, 22.2) * mm});
            skLineSegment(sketch, "E63", {"start": v(62.94, 22.2) * mm, "end": v(63.94, 22.42) * mm});
            skSolve(sketch);
        }
        {
            var Q0;
            {var subQ0=sQuery(id+"F17.wireOp",EDGE,"E61");Q0=makeQuery(id+"F17.imprint","IMPRINT",FACE,{"disambiguationData":[TD([[makeQuery(id+"F17.imprint","IMPRINT",EDGE,{"derivedFrom":subQ0}),-1.0]])]});}
            var Q1;
            Q1=sQuery(id+"F17.wireOp",EDGE,"E61");
            revolve(context, id + "F18", {"operationType" : NewBodyOperationType.ADD, "entities" : qUnion([Q0]), "axis" : qUnion([Q1]), "revolveType" : RevolveType.FULL});
        }
        {
            var Q0;
            {var subQ156=sQuery(id+"F0.wireOp",EDGE,"E0.bottom");var subQ157=makeQuery(id+"F1.opExtrude","SWEPT_FACE",FACE,{"disambiguationData":[OSD([subQ156])]});var subQ161=sQuery(id+"F0.wireOp",EDGE,"E0.right");var subQ169=sQuery(id+"F0.wireOp",EDGE,"E0.top");var subQ175=sQuery(id+"F0.wireOp",EDGE,"E0.left");Q0=makeQuery(id+"F14.boolean.opBoolean","SPLIT",FACE,{"disambiguationData":[TD([subQ157])],"derivedFrom":makeQuery(id+"F8.boolean.opBoolean","SPLIT",FACE,{"disambiguationData":[TD([subQ157])],"derivedFrom":makeQuery(id+"F5.boolean.opBoolean","SPLIT",FACE,{"disambiguationData":[TD([subQ157])],"derivedFrom":makeQuery(id+"F3.boolean.opBoolean","SPLIT",FACE,{"disambiguationData":[TD([subQ157])],"derivedFrom":makeQuery(id+"F1.opExtrude","CAP_FACE",FACE,{"disambiguationData":[OSD([subQ156,subQ169,subQ175,subQ161])],"isStart":false})})})})});}
            var sketch = newSketch(context, id + "F19", { "sketchPlane" : qUnion([Q0])});
            skLineSegment(sketch, "E64", {"start": v(75.07, -11.14) * mm, "end": v(76.46, -14.69) * mm});
            skLineSegment(sketch, "E65", {"start": v(75.66, -10.91) * mm, "end": v(77.98, -16.82) * mm});
            skLineSegment(sketch, "E66", {"start": v(76.46, -14.69) * mm, "end": v(77.98, -16.82) * mm});
            skSolve(sketch);
        }
        {
            var Q0;
            {var subQ0=sQuery(id+"F19.wireOp",EDGE,"E64");Q0=makeQuery(id+"F19.imprint","IMPRINT",FACE,{"disambiguationData":[TD([[makeQuery(id+"F19.imprint","IMPRINT",EDGE,{"derivedFrom":subQ0}),1.0]])]});}
            var Q1;
            Q1=sQuery(id+"F19.wireOp",EDGE,"E65");
            revolve(context, id + "F20", {"operationType" : NewBodyOperationType.ADD, "entities" : qUnion([Q0]), "axis" : qUnion([Q1]), "revolveType" : RevolveType.FULL});
        }
        {
            var Q0;
            {var subQ156=sQuery(id+"F0.wireOp",EDGE,"E0.bottom");var subQ157=makeQuery(id+"F1.opExtrude","SWEPT_FACE",FACE,{"disambiguationData":[OSD([subQ156])]});var subQ161=sQuery(id+"F0.wireOp",EDGE,"E0.right");var subQ169=sQuery(id+"F0.wireOp",EDGE,"E0.top");var subQ175=sQuery(id+"F0.wireOp",EDGE,"E0.left");Q0=makeQuery(id+"F14.boolean.opBoolean","SPLIT",FACE,{"disambiguationData":[TD([subQ157])],"derivedFrom":makeQuery(id+"F8.boolean.opBoolean","SPLIT",FACE,{"disambiguationData":[TD([subQ157])],"derivedFrom":makeQuery(id+"F5.boolean.opBoolean","SPLIT",FACE,{"disambiguationData":[TD([subQ157])],"derivedFrom":makeQuery(id+"F3.boolean.opBoolean","SPLIT",FACE,{"disambiguationData":[TD([subQ157])],"derivedFrom":makeQuery(id+"F1.opExtrude","CAP_FACE",FACE,{"disambiguationData":[OSD([subQ156,subQ169,subQ175,subQ161])],"isStart":false})})})})});}
            var sketch = newSketch(context, id + "F21", { "sketchPlane" : qUnion([Q0])});
            skLineSegment(sketch, "E67", {"start": v(60.57, -3.02) * mm, "end": v(58.32, -18.1) * mm});
            skLineSegment(sketch, "E68", {"start": v(58.69, -2.74) * mm, "end": v(55.5, -24.09) * mm});
            skLineSegment(sketch, "E69", {"start": v(60.57, -3.02) * mm, "end": v(58.69, -2.74) * mm});
            skLineSegment(sketch, "E70", {"start": v(58.32, -18.1) * mm, "end": v(55.5, -24.09) * mm});
            skLineSegment(sketch, "E71", {"start": v(59.63, -2.88) * mm, "end": v(51.9, -31.75) * mm});
            skSolve(sketch);
        }
        {
            var Q0;
            {var subQ3=sQuery(id+"F21.wireOp",EDGE,"E71");Q0=makeQuery(id+"F21.imprint","IMPRINT",FACE,{"disambiguationData":[TD([[makeQuery(id+"F21.imprint","IMPRINT",EDGE,{"derivedFrom":subQ3}),1.0]])]});}
            var Q1;
            {var subQ7=sQuery(id+"F21.wireOp",EDGE,"E71");Q1=makeQuery(id+"F21.imprint","IMPRINT",FACE,{"disambiguationData":[TD([[makeQuery(id+"F21.imprint","IMPRINT",EDGE,{"derivedFrom":subQ7}),-1.0]])]});}
            var Q2;
            {var subQ0=sQuery(id+"F21.wireOp",EDGE,"E70");var subQ1=sQuery(id+"F21.wireOp",EDGE,"E68");var subQ2=makeQuery(id+"F21.imprint","INTERSECT",VERTEX,{"derivedFrom":[subQ1,subQ0]});Q2=makeQuery(id+"F21.imprint","IMPRINT",FACE,{"disambiguationData":[TD([[makeQuery(id+"F21.imprint","IMPRINT",EDGE,{"disambiguationData":[TD([[subQ2,1.0]])],"derivedFrom":subQ1}),1.0]])]});}
            var Q3;
            Q3=sQuery(id+"F21.wireOp",EDGE,"E68");
            revolve(context, id + "F22", {"operationType" : NewBodyOperationType.ADD, "entities" : qUnion([Q0, Q1, Q2]), "axis" : qUnion([Q3]), "revolveType" : RevolveType.FULL});
        }
        {
            var Q0;
            {var subQ156=sQuery(id+"F0.wireOp",EDGE,"E0.bottom");var subQ157=makeQuery(id+"F1.opExtrude","SWEPT_FACE",FACE,{"disambiguationData":[OSD([subQ156])]});var subQ161=sQuery(id+"F0.wireOp",EDGE,"E0.right");var subQ169=sQuery(id+"F0.wireOp",EDGE,"E0.top");var subQ175=sQuery(id+"F0.wireOp",EDGE,"E0.left");Q0=makeQuery(id+"F14.boolean.opBoolean","SPLIT",FACE,{"disambiguationData":[TD([subQ157])],"derivedFrom":makeQuery(id+"F8.boolean.opBoolean","SPLIT",FACE,{"disambiguationData":[TD([subQ157])],"derivedFrom":makeQuery(id+"F5.boolean.opBoolean","SPLIT",FACE,{"disambiguationData":[TD([subQ157])],"derivedFrom":makeQuery(id+"F3.boolean.opBoolean","SPLIT",FACE,{"disambiguationData":[TD([subQ157])],"derivedFrom":makeQuery(id+"F1.opExtrude","CAP_FACE",FACE,{"disambiguationData":[OSD([subQ156,subQ169,subQ175,subQ161])],"isStart":false})})})})});}
            var sketch = newSketch(context, id + "F23", { "sketchPlane" : qUnion([Q0])});
            skLineSegment(sketch, "E72", {"start": v(61.89, -6.17) * mm, "end": v(54.98, -5.14) * mm});
            skLineSegment(sketch, "E73", {"start": v(54.98, -5.14) * mm, "end": v(54.23, -10.17) * mm});
            skLineSegment(sketch, "E74", {"start": v(54.23, -10.17) * mm, "end": v(61.14, -11.2) * mm});
            skLineSegment(sketch, "E75", {"start": v(61.89, -6.17) * mm, "end": v(61.14, -11.2) * mm});
            skSolve(sketch);
        }
        {
            var Q0;
            {var subQ0=sQuery(id+"F23.wireOp",EDGE,"E73");Q0=makeQuery(id+"F23.imprint","IMPRINT",FACE,{"disambiguationData":[TD([[makeQuery(id+"F23.imprint","IMPRINT",EDGE,{"derivedFrom":subQ0}),1.0]])]});}
            var Q1;
            {var subQ0=sQuery(id+"F23.wireOp",EDGE,"E75");Q1=makeQuery(id+"F23.imprint","IMPRINT",FACE,{"disambiguationData":[TD([[makeQuery(id+"F23.imprint","IMPRINT",EDGE,{"derivedFrom":subQ0}),-1.0]])]});}
            extrude(context, id + "F24", {"entities" : qUnion([Q0, Q1]), "operationType" : NewBodyOperationType.ADD, "depth" : 2.3 * mm, "offsetDistance" : 25.4 * mm});
        }
        {
            var Q0;
            {var subQ156=sQuery(id+"F0.wireOp",EDGE,"E0.bottom");var subQ157=makeQuery(id+"F1.opExtrude","SWEPT_FACE",FACE,{"disambiguationData":[OSD([subQ156])]});var subQ161=sQuery(id+"F0.wireOp",EDGE,"E0.right");var subQ169=sQuery(id+"F0.wireOp",EDGE,"E0.top");var subQ175=sQuery(id+"F0.wireOp",EDGE,"E0.left");Q0=makeQuery(id+"F14.boolean.opBoolean","SPLIT",FACE,{"disambiguationData":[TD([subQ157])],"derivedFrom":makeQuery(id+"F8.boolean.opBoolean","SPLIT",FACE,{"disambiguationData":[TD([subQ157])],"derivedFrom":makeQuery(id+"F5.boolean.opBoolean","SPLIT",FACE,{"disambiguationData":[TD([subQ157])],"derivedFrom":makeQuery(id+"F3.boolean.opBoolean","SPLIT",FACE,{"disambiguationData":[TD([subQ157])],"derivedFrom":makeQuery(id+"F1.opExtrude","CAP_FACE",FACE,{"disambiguationData":[OSD([subQ156,subQ169,subQ175,subQ161])],"isStart":false})})})})});}
            var sketch = newSketch(context, id + "F25", { "sketchPlane" : qUnion([Q0])});
            skLineSegment(sketch, "E76", {"start": v(54.6, -7.65) * mm, "end": v(52.1, -7.28) * mm});
            skLineSegment(sketch, "E77", {"start": v(52.1, -7.28) * mm, "end": v(52.18, -6.65) * mm});
            skLineSegment(sketch, "E78", {"start": v(52.18, -6.65) * mm, "end": v(54.7, -7.03) * mm});
            skLineSegment(sketch, "E79", {"start": v(52.83, -6.75) * mm, "end": v(53.2, -4.24) * mm});
            skLineSegment(sketch, "E80", {"start": v(53.2, -4.24) * mm, "end": v(54.46, -4.42) * mm});
            skLineSegment(sketch, "E81", {"start": v(54.46, -4.42) * mm, "end": v(54.09, -6.94) * mm});
            skSolve(sketch);
        }
        {
            var Q0;
            {var subQ0=sQuery(id+"F25.wireOp",EDGE,"E79");Q0=makeQuery(id+"F25.imprint","IMPRINT",FACE,{"disambiguationData":[TD([[makeQuery(id+"F25.imprint","IMPRINT",EDGE,{"derivedFrom":subQ0}),-1.0]])]});}
            var Q1;
            {var subQ4=sQuery(id+"F25.wireOp",EDGE,"E76");Q1=makeQuery(id+"F25.imprint","IMPRINT",FACE,{"disambiguationData":[TD([[makeQuery(id+"F25.imprint","IMPRINT",EDGE,{"derivedFrom":subQ4}),-1.0]])]});}
            var Q2;
            Q2=sQuery(id+"F25.wireOp",EDGE,"E76");
            revolve(context, id + "F26", {"operationType" : NewBodyOperationType.ADD, "entities" : qUnion([Q0, Q1]), "axis" : qUnion([Q2]), "revolveType" : RevolveType.FULL});
        }
        {
            var Q0;
            {var subQ156=sQuery(id+"F0.wireOp",EDGE,"E0.bottom");var subQ157=makeQuery(id+"F1.opExtrude","SWEPT_FACE",FACE,{"disambiguationData":[OSD([subQ156])]});var subQ161=sQuery(id+"F0.wireOp",EDGE,"E0.right");var subQ169=sQuery(id+"F0.wireOp",EDGE,"E0.top");var subQ175=sQuery(id+"F0.wireOp",EDGE,"E0.left");Q0=makeQuery(id+"F14.boolean.opBoolean","SPLIT",FACE,{"disambiguationData":[TD([subQ157])],"derivedFrom":makeQuery(id+"F8.boolean.opBoolean","SPLIT",FACE,{"disambiguationData":[TD([subQ157])],"derivedFrom":makeQuery(id+"F5.boolean.opBoolean","SPLIT",FACE,{"disambiguationData":[TD([subQ157])],"derivedFrom":makeQuery(id+"F3.boolean.opBoolean","SPLIT",FACE,{"disambiguationData":[TD([subQ157])],"derivedFrom":makeQuery(id+"F1.opExtrude","CAP_FACE",FACE,{"disambiguationData":[OSD([subQ156,subQ169,subQ175,subQ161])],"isStart":false})})})})});}
            var sketch = newSketch(context, id + "F27", { "sketchPlane" : qUnion([Q0])});
            skCircle(sketch, "E82", {"center": v(-83.82, 26.67) * mm, "radius": 2.54 * mm});
            skCircle(sketch, "E83", {"center": v(83.82, 26.67) * mm, "radius": 2.54 * mm});
            skSolve(sketch);
        }
        {
            var Q0;
            Q0=makeQuery(id+"F27.imprint","IMPRINT",FACE,{"disambiguationData":[TD([[makeQuery(id+"F27.imprint","IMPRINT",EDGE,{"derivedFrom":sQuery(id+"F27.wireOp",EDGE,"E82")}),1.0]])]});
            var Q1;
            Q1=makeQuery(id+"F27.imprint","IMPRINT",FACE,{"disambiguationData":[TD([[makeQuery(id+"F27.imprint","IMPRINT",EDGE,{"derivedFrom":sQuery(id+"F27.wireOp",EDGE,"E83")}),1.0]])]});
            extrude(context, id + "F28", {"entities" : qUnion([Q0, Q1]), "operationType" : NewBodyOperationType.REMOVE, "endBound" : BoundingType.UP_TO_NEXT, "oppositeDirection" : true, "depth" : 25.4 * mm, "offsetDistance" : 25.4 * mm});
        }
        {
            var Q0;
            Q0=makeQuery(id+"F1.opExtrude","SWEPT_FACE",FACE,{"disambiguationData":[OSD([sQuery(id+"F0.wireOp",EDGE,"E0.left")])]});
            var sketch = newSketch(context, id + "F29", { "sketchPlane" : qUnion([Q0])});
            skLineSegment(sketch, "E84.bottom", {"start": v(-31.75, 0) * mm, "end": v(31.75, 0) * mm});
            skLineSegment(sketch, "E84.top", {"start": v(-31.75, -7.62) * mm, "end": v(31.75, -7.62) * mm});
            skLineSegment(sketch, "E84.left", {"start": v(-31.75, 0) * mm, "end": v(-31.75, -7.62) * mm});
            skLineSegment(sketch, "E84.right", {"start": v(31.75, 0) * mm, "end": v(31.75, -7.62) * mm});
            skSolve(sketch);
        }
        {
            var Q0;
            Q0=makeQuery(id+"F29.imprint","IMPRINT",FACE,{"disambiguationData":[TD([[makeQuery(id+"F29.imprint","IMPRINT",EDGE,{"derivedFrom":sQuery(id+"F29.wireOp",EDGE,"E84.bottom")}),1.0]])]});
            extrude(context, id + "F30", {"entities" : qUnion([Q0]), "operationType" : NewBodyOperationType.REMOVE, "oppositeDirection" : true, "depth" : 177.8 * mm, "offsetDistance" : 25.4 * mm});
        }
    });
